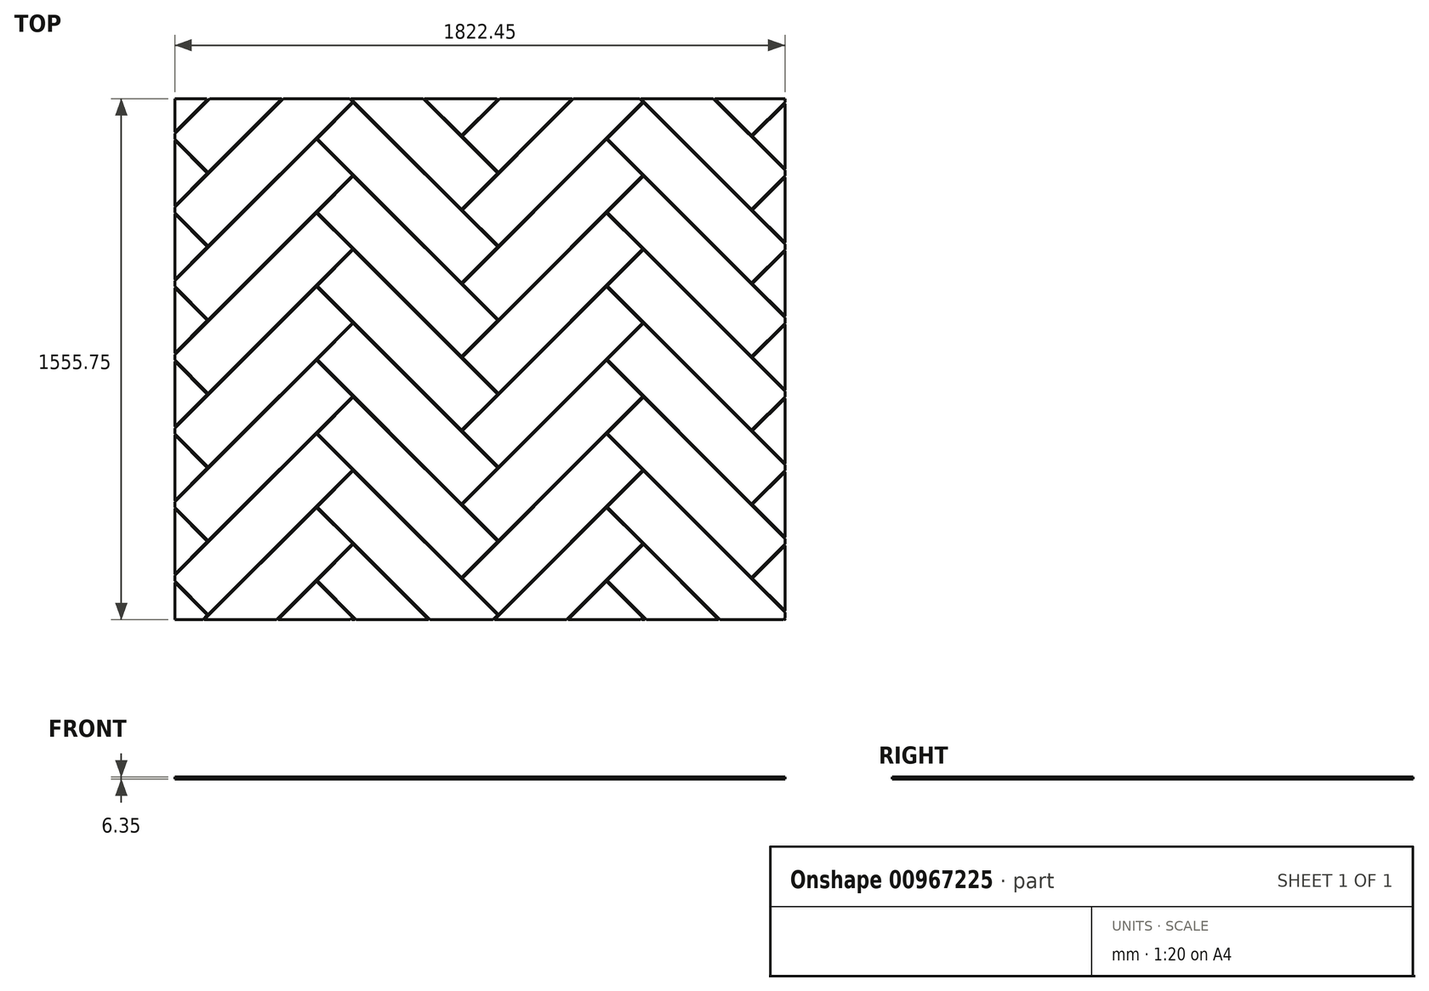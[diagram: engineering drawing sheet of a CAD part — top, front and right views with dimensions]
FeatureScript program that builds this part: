
annotation { "Feature Type Name" : "Feature", "Feature Type Description" : "" }
export const myFeature = defineFeature(function(context is Context, id is Id, definition is map)
    precondition{}
    {
        {
            var Q0;
            Q0=qCreatedBy(makeId("Top.planeOp"),FACE);
            var sketch = newSketch(context, id + "F0", { "sketchPlane" : qUnion([Q0])});
            skLineSegment(sketch, "E0.bottom", {"start": v(0, 0) * mm, "end": v(609.6, 0) * mm});
            skLineSegment(sketch, "E0.top", {"start": v(0, 152.4) * mm, "end": v(609.6, 152.4) * mm});
            skLineSegment(sketch, "E0.left", {"start": v(0, 0) * mm, "end": v(0, 152.4) * mm});
            skLineSegment(sketch, "E0.right", {"start": v(609.6, 0) * mm, "end": v(609.6, 152.4) * mm});
            skLineSegment(sketch, "E1.bottom", {"start": v(152.4, 155.57) * mm, "end": v(152.4, 765.17) * mm});
            skLineSegment(sketch, "E1.top", {"start": v(0, 155.58) * mm, "end": v(0, 765.17) * mm});
            skLineSegment(sketch, "E1.left", {"start": v(152.4, 155.57) * mm, "end": v(0, 155.57) * mm});
            skLineSegment(sketch, "E1.right", {"start": v(152.4, 765.17) * mm, "end": v(0, 765.17) * mm});
            skLineSegment(sketch, "E2.bottom", {"start": v(155.58, 155.57) * mm, "end": v(765.17, 155.57) * mm});
            skLineSegment(sketch, "E2.top", {"start": v(155.58, 307.98) * mm, "end": v(765.17, 307.97) * mm});
            skLineSegment(sketch, "E2.left", {"start": v(155.58, 155.58) * mm, "end": v(155.58, 307.98) * mm});
            skLineSegment(sketch, "E2.right", {"start": v(765.17, 155.57) * mm, "end": v(765.17, 307.97) * mm});
            skLineSegment(sketch, "E3.bottom", {"start": v(307.98, 311.15) * mm, "end": v(307.98, 920.75) * mm});
            skLineSegment(sketch, "E3.top", {"start": v(155.58, 311.15) * mm, "end": v(155.58, 920.75) * mm});
            skLineSegment(sketch, "E3.left", {"start": v(307.98, 311.15) * mm, "end": v(155.58, 311.15) * mm});
            skLineSegment(sketch, "E3.right", {"start": v(307.98, 920.75) * mm, "end": v(155.58, 920.75) * mm});
            skLineSegment(sketch, "E4.0.1.0", {"start": v(-612.78, 612.78) * mm, "end": v(-3.18, 612.78) * mm});
            skLineSegment(sketch, "E4.0.1.1", {"start": v(-460.37, 768.35) * mm, "end": v(-612.77, 768.35) * mm});
            skLineSegment(sketch, "E4.0.1.2", {"start": v(-457.2, 768.35) * mm, "end": v(-457.2, 920.75) * mm});
            skLineSegment(sketch, "E4.0.1.3", {"start": v(-304.8, 923.92) * mm, "end": v(-457.2, 923.92) * mm});
            skLineSegment(sketch, "E4.0.1.4", {"start": v(-457.2, 768.35) * mm, "end": v(152.4, 768.35) * mm});
            skLineSegment(sketch, "E4.0.1.5", {"start": v(-460.37, 768.35) * mm, "end": v(-460.37, 1377.95) * mm});
            skLineSegment(sketch, "E4.0.1.6", {"start": v(-457.2, 920.75) * mm, "end": v(152.4, 920.75) * mm});
            skLineSegment(sketch, "E4.0.1.7", {"start": v(-304.8, 1533.52) * mm, "end": v(-457.2, 1533.52) * mm});
            skLineSegment(sketch, "E4.0.1.8", {"start": v(-612.78, 768.35) * mm, "end": v(-612.77, 1377.95) * mm});
            skLineSegment(sketch, "E4.0.1.9", {"start": v(-457.2, 923.92) * mm, "end": v(-457.2, 1533.52) * mm});
            skLineSegment(sketch, "E4.0.1.10", {"start": v(-3.18, 612.78) * mm, "end": v(-3.18, 765.17) * mm});
            skLineSegment(sketch, "E4.0.1.11", {"start": v(-304.8, 923.92) * mm, "end": v(-304.8, 1533.52) * mm});
            skLineSegment(sketch, "E4.0.1.12", {"start": v(-612.78, 612.78) * mm, "end": v(-612.78, 765.17) * mm});
            skLineSegment(sketch, "E4.0.1.13", {"start": v(-460.37, 1377.95) * mm, "end": v(-612.77, 1377.95) * mm});
            skLineSegment(sketch, "E4.0.1.14", {"start": v(152.4, 768.35) * mm, "end": v(152.4, 920.75) * mm});
            skLineSegment(sketch, "E4.0.1.15", {"start": v(-612.77, 765.17) * mm, "end": v(-3.17, 765.17) * mm});
            skLineSegment(sketch, "E4.1.0.0", {"start": v(311.15, 311.15) * mm, "end": v(920.75, 311.15) * mm});
            skLineSegment(sketch, "E4.1.0.1", {"start": v(463.55, 466.72) * mm, "end": v(311.15, 466.72) * mm});
            skLineSegment(sketch, "E4.1.0.2", {"start": v(466.73, 466.72) * mm, "end": v(466.73, 619.12) * mm});
            skLineSegment(sketch, "E4.1.0.3", {"start": v(619.13, 622.3) * mm, "end": v(466.73, 622.3) * mm});
            skLineSegment(sketch, "E4.1.0.4", {"start": v(466.73, 466.72) * mm, "end": v(1076.33, 466.72) * mm});
            skLineSegment(sketch, "E4.1.0.5", {"start": v(463.55, 466.72) * mm, "end": v(463.55, 1076.32) * mm});
            skLineSegment(sketch, "E4.1.0.6", {"start": v(466.73, 619.12) * mm, "end": v(1076.33, 619.12) * mm});
            skLineSegment(sketch, "E4.1.0.7", {"start": v(619.13, 1231.9) * mm, "end": v(466.73, 1231.9) * mm});
            skLineSegment(sketch, "E4.1.0.8", {"start": v(311.15, 466.72) * mm, "end": v(311.15, 1076.32) * mm});
            skLineSegment(sketch, "E4.1.0.9", {"start": v(466.73, 622.3) * mm, "end": v(466.73, 1231.9) * mm});
            skLineSegment(sketch, "E4.1.0.10", {"start": v(920.75, 311.15) * mm, "end": v(920.75, 463.55) * mm});
            skLineSegment(sketch, "E4.1.0.11", {"start": v(619.13, 622.3) * mm, "end": v(619.13, 1231.9) * mm});
            skLineSegment(sketch, "E4.1.0.12", {"start": v(311.15, 311.15) * mm, "end": v(311.15, 463.55) * mm});
            skLineSegment(sketch, "E4.1.0.13", {"start": v(463.55, 1076.32) * mm, "end": v(311.15, 1076.32) * mm});
            skLineSegment(sketch, "E4.1.0.14", {"start": v(1076.32, 466.72) * mm, "end": v(1076.32, 619.12) * mm});
            skLineSegment(sketch, "E4.1.0.15", {"start": v(311.15, 463.55) * mm, "end": v(920.75, 463.55) * mm});
            skLineSegment(sketch, "E4.1.1.0", {"start": v(-301.62, 923.92) * mm, "end": v(307.98, 923.92) * mm});
            skLineSegment(sketch, "E4.1.1.1", {"start": v(-149.22, 1079.5) * mm, "end": v(-301.62, 1079.5) * mm});
            skLineSegment(sketch, "E4.1.1.2", {"start": v(-146.05, 1079.5) * mm, "end": v(-146.05, 1231.9) * mm});
            skLineSegment(sketch, "E4.1.1.3", {"start": v(6.35, 1235.07) * mm, "end": v(-146.05, 1235.07) * mm});
            skLineSegment(sketch, "E4.1.1.4", {"start": v(-146.05, 1079.5) * mm, "end": v(463.55, 1079.5) * mm});
            skLineSegment(sketch, "E4.1.1.5", {"start": v(-149.22, 1079.5) * mm, "end": v(-149.22, 1689.1) * mm});
            skLineSegment(sketch, "E4.1.1.6", {"start": v(-146.05, 1231.9) * mm, "end": v(463.55, 1231.9) * mm});
            skLineSegment(sketch, "E4.1.1.7", {"start": v(6.35, 1844.67) * mm, "end": v(-146.05, 1844.67) * mm});
            skLineSegment(sketch, "E4.1.1.8", {"start": v(-301.62, 1079.5) * mm, "end": v(-301.62, 1689.1) * mm});
            skLineSegment(sketch, "E4.1.1.9", {"start": v(-146.05, 1235.07) * mm, "end": v(-146.05, 1844.67) * mm});
            skLineSegment(sketch, "E4.1.1.10", {"start": v(307.98, 923.92) * mm, "end": v(307.98, 1076.32) * mm});
            skLineSegment(sketch, "E4.1.1.11", {"start": v(6.35, 1235.07) * mm, "end": v(6.35, 1844.67) * mm});
            skLineSegment(sketch, "E4.1.1.12", {"start": v(-301.62, 923.92) * mm, "end": v(-301.62, 1076.32) * mm});
            skLineSegment(sketch, "E4.1.1.13", {"start": v(-149.22, 1689.1) * mm, "end": v(-301.62, 1689.1) * mm});
            skLineSegment(sketch, "E4.1.1.14", {"start": v(463.55, 1079.5) * mm, "end": v(463.55, 1231.9) * mm});
            skLineSegment(sketch, "E4.1.1.15", {"start": v(-301.62, 1076.32) * mm, "end": v(307.98, 1076.32) * mm});
            skLineSegment(sketch, "E4.2.0.0", {"start": v(622.3, 622.3) * mm, "end": v(1231.9, 622.3) * mm});
            skLineSegment(sketch, "E4.2.0.1", {"start": v(774.7, 777.87) * mm, "end": v(622.3, 777.87) * mm});
            skLineSegment(sketch, "E4.2.0.2", {"start": v(777.88, 777.87) * mm, "end": v(777.88, 930.27) * mm});
            skLineSegment(sketch, "E4.2.0.3", {"start": v(930.28, 933.45) * mm, "end": v(777.88, 933.45) * mm});
            skLineSegment(sketch, "E4.2.0.4", {"start": v(777.88, 777.87) * mm, "end": v(1387.47, 777.87) * mm});
            skLineSegment(sketch, "E4.2.0.5", {"start": v(774.7, 777.87) * mm, "end": v(774.7, 1387.47) * mm});
            skLineSegment(sketch, "E4.2.0.6", {"start": v(777.88, 930.27) * mm, "end": v(1387.47, 930.27) * mm});
            skLineSegment(sketch, "E4.2.0.7", {"start": v(930.28, 1543.05) * mm, "end": v(777.88, 1543.05) * mm});
            skLineSegment(sketch, "E4.2.0.8", {"start": v(622.3, 777.87) * mm, "end": v(622.3, 1387.47) * mm});
            skLineSegment(sketch, "E4.2.0.9", {"start": v(777.88, 933.45) * mm, "end": v(777.88, 1543.05) * mm});
            skLineSegment(sketch, "E4.2.0.10", {"start": v(1231.9, 622.3) * mm, "end": v(1231.9, 774.7) * mm});
            skLineSegment(sketch, "E4.2.0.11", {"start": v(930.28, 933.45) * mm, "end": v(930.28, 1543.05) * mm});
            skLineSegment(sketch, "E4.2.0.12", {"start": v(622.3, 622.3) * mm, "end": v(622.3, 774.7) * mm});
            skLineSegment(sketch, "E4.2.0.13", {"start": v(774.7, 1387.47) * mm, "end": v(622.3, 1387.47) * mm});
            skLineSegment(sketch, "E4.2.0.14", {"start": v(1387.47, 777.87) * mm, "end": v(1387.47, 930.27) * mm});
            skLineSegment(sketch, "E4.2.0.15", {"start": v(622.3, 774.7) * mm, "end": v(1231.9, 774.7) * mm});
            skLineSegment(sketch, "E4.2.1.0", {"start": v(9.53, 1235.07) * mm, "end": v(619.13, 1235.07) * mm});
            skLineSegment(sketch, "E4.2.1.1", {"start": v(161.93, 1390.65) * mm, "end": v(9.53, 1390.65) * mm});
            skLineSegment(sketch, "E4.2.1.2", {"start": v(165.1, 1390.65) * mm, "end": v(165.1, 1543.05) * mm});
            skLineSegment(sketch, "E4.2.1.3", {"start": v(317.5, 1546.22) * mm, "end": v(165.1, 1546.22) * mm});
            skLineSegment(sketch, "E4.2.1.4", {"start": v(165.1, 1390.65) * mm, "end": v(774.7, 1390.65) * mm});
            skLineSegment(sketch, "E4.2.1.5", {"start": v(161.93, 1390.65) * mm, "end": v(161.93, 2000.25) * mm});
            skLineSegment(sketch, "E4.2.1.6", {"start": v(165.1, 1543.05) * mm, "end": v(774.7, 1543.05) * mm});
            skLineSegment(sketch, "E4.2.1.7", {"start": v(317.5, 2155.82) * mm, "end": v(165.1, 2155.82) * mm});
            skLineSegment(sketch, "E4.2.1.8", {"start": v(9.53, 1390.65) * mm, "end": v(9.53, 2000.25) * mm});
            skLineSegment(sketch, "E4.2.1.9", {"start": v(165.1, 1546.22) * mm, "end": v(165.1, 2155.82) * mm});
            skLineSegment(sketch, "E4.2.1.10", {"start": v(619.13, 1235.07) * mm, "end": v(619.13, 1387.47) * mm});
            skLineSegment(sketch, "E4.2.1.11", {"start": v(317.5, 1546.22) * mm, "end": v(317.5, 2155.82) * mm});
            skLineSegment(sketch, "E4.2.1.12", {"start": v(9.53, 1235.07) * mm, "end": v(9.53, 1387.47) * mm});
            skLineSegment(sketch, "E4.2.1.13", {"start": v(161.93, 2000.25) * mm, "end": v(9.53, 2000.25) * mm});
            skLineSegment(sketch, "E4.2.1.14", {"start": v(774.7, 1390.65) * mm, "end": v(774.7, 1543.05) * mm});
            skLineSegment(sketch, "E4.2.1.15", {"start": v(9.53, 1387.47) * mm, "end": v(619.13, 1387.47) * mm});
            skLineSegment(sketch, "E4.direction1", {"start": v(0, 0) * mm, "end": v(311.15, 311.15) * mm, "construction": true});
            skLineSegment(sketch, "E4.direction2", {"start": v(0, 0) * mm, "end": v(-612.78, 612.78) * mm, "construction": true});
            skLineSegment(sketch, "E5.0.3.0", {"start": v(933.45, 933.45) * mm, "end": v(1543.05, 933.45) * mm});
            skLineSegment(sketch, "E5.3.3.0", {"start": v(1085.85, 1089.02) * mm, "end": v(933.45, 1089.02) * mm});
            skLineSegment(sketch, "E5.6.3.0", {"start": v(1089.03, 1089.02) * mm, "end": v(1089.03, 1241.42) * mm});
            skLineSegment(sketch, "E5.9.3.0", {"start": v(1241.43, 1244.6) * mm, "end": v(1089.03, 1244.6) * mm});
            skLineSegment(sketch, "E5.12.3.0", {"start": v(1089.03, 1089.02) * mm, "end": v(1698.62, 1089.02) * mm});
            skLineSegment(sketch, "E5.15.3.0", {"start": v(1085.85, 1089.02) * mm, "end": v(1085.85, 1698.62) * mm});
            skLineSegment(sketch, "E5.18.3.0", {"start": v(1089.03, 1241.42) * mm, "end": v(1698.62, 1241.42) * mm});
            skLineSegment(sketch, "E5.21.3.0", {"start": v(1241.43, 1854.2) * mm, "end": v(1089.03, 1854.2) * mm});
            skLineSegment(sketch, "E5.24.3.0", {"start": v(933.45, 1089.02) * mm, "end": v(933.45, 1698.62) * mm});
            skLineSegment(sketch, "E5.27.3.0", {"start": v(1089.03, 1244.6) * mm, "end": v(1089.03, 1854.2) * mm});
            skLineSegment(sketch, "E5.30.3.0", {"start": v(1543.05, 933.45) * mm, "end": v(1543.05, 1085.85) * mm});
            skLineSegment(sketch, "E5.33.3.0", {"start": v(1241.43, 1244.6) * mm, "end": v(1241.43, 1854.2) * mm});
            skLineSegment(sketch, "E5.36.3.0", {"start": v(933.45, 933.45) * mm, "end": v(933.45, 1085.85) * mm});
            skLineSegment(sketch, "E5.39.3.0", {"start": v(1085.85, 1698.62) * mm, "end": v(933.45, 1698.62) * mm});
            skLineSegment(sketch, "E5.42.3.0", {"start": v(1698.62, 1089.02) * mm, "end": v(1698.62, 1241.42) * mm});
            skLineSegment(sketch, "E5.45.3.0", {"start": v(933.45, 1085.85) * mm, "end": v(1543.05, 1085.85) * mm});
            skLineSegment(sketch, "E5.0.3.1", {"start": v(320.68, 1546.22) * mm, "end": v(930.28, 1546.22) * mm});
            skLineSegment(sketch, "E5.3.3.1", {"start": v(473.08, 1701.8) * mm, "end": v(320.68, 1701.8) * mm});
            skLineSegment(sketch, "E5.6.3.1", {"start": v(476.25, 1701.8) * mm, "end": v(476.25, 1854.2) * mm});
            skLineSegment(sketch, "E5.9.3.1", {"start": v(628.65, 1857.37) * mm, "end": v(476.25, 1857.37) * mm});
            skLineSegment(sketch, "E5.12.3.1", {"start": v(476.25, 1701.8) * mm, "end": v(1085.85, 1701.8) * mm});
            skLineSegment(sketch, "E5.15.3.1", {"start": v(473.08, 1701.8) * mm, "end": v(473.08, 2311.4) * mm});
            skLineSegment(sketch, "E5.18.3.1", {"start": v(476.25, 1854.2) * mm, "end": v(1085.85, 1854.2) * mm});
            skLineSegment(sketch, "E5.21.3.1", {"start": v(628.65, 2466.97) * mm, "end": v(476.25, 2466.97) * mm});
            skLineSegment(sketch, "E5.24.3.1", {"start": v(320.68, 1701.8) * mm, "end": v(320.68, 2311.4) * mm});
            skLineSegment(sketch, "E5.27.3.1", {"start": v(476.25, 1857.37) * mm, "end": v(476.25, 2466.97) * mm});
            skLineSegment(sketch, "E5.30.3.1", {"start": v(930.28, 1546.22) * mm, "end": v(930.28, 1698.62) * mm});
            skLineSegment(sketch, "E5.33.3.1", {"start": v(628.65, 1857.37) * mm, "end": v(628.65, 2466.97) * mm});
            skLineSegment(sketch, "E5.36.3.1", {"start": v(320.68, 1546.22) * mm, "end": v(320.68, 1698.62) * mm});
            skLineSegment(sketch, "E5.39.3.1", {"start": v(473.08, 2311.4) * mm, "end": v(320.68, 2311.4) * mm});
            skLineSegment(sketch, "E5.42.3.1", {"start": v(1085.85, 1701.8) * mm, "end": v(1085.85, 1854.2) * mm});
            skLineSegment(sketch, "E5.45.3.1", {"start": v(320.68, 1698.62) * mm, "end": v(930.28, 1698.62) * mm});
            skLineSegment(sketch, "E5.0.4.0", {"start": v(1244.6, 1244.6) * mm, "end": v(1854.2, 1244.6) * mm});
            skLineSegment(sketch, "E5.3.4.0", {"start": v(1397, 1400.17) * mm, "end": v(1244.6, 1400.17) * mm});
            skLineSegment(sketch, "E5.6.4.0", {"start": v(1400.18, 1400.17) * mm, "end": v(1400.18, 1552.57) * mm});
            skLineSegment(sketch, "E5.9.4.0", {"start": v(1552.58, 1555.75) * mm, "end": v(1400.18, 1555.75) * mm});
            skLineSegment(sketch, "E5.12.4.0", {"start": v(1400.18, 1400.17) * mm, "end": v(2009.78, 1400.17) * mm});
            skLineSegment(sketch, "E5.15.4.0", {"start": v(1397, 1400.17) * mm, "end": v(1397, 2009.77) * mm});
            skLineSegment(sketch, "E5.18.4.0", {"start": v(1400.18, 1552.57) * mm, "end": v(2009.78, 1552.57) * mm});
            skLineSegment(sketch, "E5.21.4.0", {"start": v(1552.58, 2165.35) * mm, "end": v(1400.18, 2165.35) * mm});
            skLineSegment(sketch, "E5.24.4.0", {"start": v(1244.6, 1400.17) * mm, "end": v(1244.6, 2009.77) * mm});
            skLineSegment(sketch, "E5.27.4.0", {"start": v(1400.18, 1555.75) * mm, "end": v(1400.18, 2165.35) * mm});
            skLineSegment(sketch, "E5.30.4.0", {"start": v(1854.2, 1244.6) * mm, "end": v(1854.2, 1397) * mm});
            skLineSegment(sketch, "E5.33.4.0", {"start": v(1552.58, 1555.75) * mm, "end": v(1552.58, 2165.35) * mm});
            skLineSegment(sketch, "E5.36.4.0", {"start": v(1244.6, 1244.6) * mm, "end": v(1244.6, 1397) * mm});
            skLineSegment(sketch, "E5.39.4.0", {"start": v(1397, 2009.77) * mm, "end": v(1244.6, 2009.77) * mm});
            skLineSegment(sketch, "E5.42.4.0", {"start": v(2009.78, 1400.17) * mm, "end": v(2009.78, 1552.57) * mm});
            skLineSegment(sketch, "E5.45.4.0", {"start": v(1244.6, 1397) * mm, "end": v(1854.2, 1397) * mm});
            skLineSegment(sketch, "E5.0.4.1", {"start": v(631.83, 1857.37) * mm, "end": v(1241.43, 1857.37) * mm});
            skLineSegment(sketch, "E5.3.4.1", {"start": v(784.23, 2012.95) * mm, "end": v(631.83, 2012.95) * mm});
            skLineSegment(sketch, "E5.6.4.1", {"start": v(787.4, 2012.95) * mm, "end": v(787.4, 2165.35) * mm});
            skLineSegment(sketch, "E5.9.4.1", {"start": v(939.8, 2168.52) * mm, "end": v(787.4, 2168.52) * mm});
            skLineSegment(sketch, "E5.12.4.1", {"start": v(787.4, 2012.95) * mm, "end": v(1397, 2012.95) * mm});
            skLineSegment(sketch, "E5.15.4.1", {"start": v(784.23, 2012.95) * mm, "end": v(784.23, 2622.55) * mm});
            skLineSegment(sketch, "E5.18.4.1", {"start": v(787.4, 2165.35) * mm, "end": v(1397, 2165.35) * mm});
            skLineSegment(sketch, "E5.21.4.1", {"start": v(939.8, 2778.12) * mm, "end": v(787.4, 2778.12) * mm});
            skLineSegment(sketch, "E5.24.4.1", {"start": v(631.83, 2012.95) * mm, "end": v(631.83, 2622.55) * mm});
            skLineSegment(sketch, "E5.27.4.1", {"start": v(787.4, 2168.52) * mm, "end": v(787.4, 2778.12) * mm});
            skLineSegment(sketch, "E5.30.4.1", {"start": v(1241.43, 1857.37) * mm, "end": v(1241.43, 2009.77) * mm});
            skLineSegment(sketch, "E5.33.4.1", {"start": v(939.8, 2168.52) * mm, "end": v(939.8, 2778.12) * mm});
            skLineSegment(sketch, "E5.36.4.1", {"start": v(631.83, 1857.37) * mm, "end": v(631.83, 2009.77) * mm});
            skLineSegment(sketch, "E5.39.4.1", {"start": v(784.23, 2622.55) * mm, "end": v(631.83, 2622.55) * mm});
            skLineSegment(sketch, "E5.42.4.1", {"start": v(1397, 2012.95) * mm, "end": v(1397, 2165.35) * mm});
            skLineSegment(sketch, "E5.45.4.1", {"start": v(631.83, 2009.77) * mm, "end": v(1241.43, 2009.77) * mm});
            skLineSegment(sketch, "E5.0.5.0", {"start": v(1555.75, 1555.75) * mm, "end": v(2165.35, 1555.75) * mm});
            skLineSegment(sketch, "E5.3.5.0", {"start": v(1708.15, 1711.32) * mm, "end": v(1555.75, 1711.32) * mm});
            skLineSegment(sketch, "E5.6.5.0", {"start": v(1711.33, 1711.32) * mm, "end": v(1711.33, 1863.72) * mm});
            skLineSegment(sketch, "E5.9.5.0", {"start": v(1863.73, 1866.9) * mm, "end": v(1711.33, 1866.9) * mm});
            skLineSegment(sketch, "E5.12.5.0", {"start": v(1711.33, 1711.32) * mm, "end": v(2320.92, 1711.32) * mm});
            skLineSegment(sketch, "E5.15.5.0", {"start": v(1708.15, 1711.32) * mm, "end": v(1708.15, 2320.92) * mm});
            skLineSegment(sketch, "E5.18.5.0", {"start": v(1711.33, 1863.72) * mm, "end": v(2320.92, 1863.72) * mm});
            skLineSegment(sketch, "E5.21.5.0", {"start": v(1863.73, 2476.5) * mm, "end": v(1711.33, 2476.5) * mm});
            skLineSegment(sketch, "E5.24.5.0", {"start": v(1555.75, 1711.32) * mm, "end": v(1555.75, 2320.92) * mm});
            skLineSegment(sketch, "E5.27.5.0", {"start": v(1711.33, 1866.9) * mm, "end": v(1711.33, 2476.5) * mm});
            skLineSegment(sketch, "E5.30.5.0", {"start": v(2165.35, 1555.75) * mm, "end": v(2165.35, 1708.15) * mm});
            skLineSegment(sketch, "E5.33.5.0", {"start": v(1863.73, 1866.9) * mm, "end": v(1863.73, 2476.5) * mm});
            skLineSegment(sketch, "E5.36.5.0", {"start": v(1555.75, 1555.75) * mm, "end": v(1555.75, 1708.15) * mm});
            skLineSegment(sketch, "E5.39.5.0", {"start": v(1708.15, 2320.92) * mm, "end": v(1555.75, 2320.92) * mm});
            skLineSegment(sketch, "E5.42.5.0", {"start": v(2320.92, 1711.32) * mm, "end": v(2320.92, 1863.72) * mm});
            skLineSegment(sketch, "E5.45.5.0", {"start": v(1555.75, 1708.15) * mm, "end": v(2165.35, 1708.15) * mm});
            skLineSegment(sketch, "E5.0.5.1", {"start": v(942.98, 2168.52) * mm, "end": v(1552.58, 2168.52) * mm});
            skLineSegment(sketch, "E5.3.5.1", {"start": v(1095.38, 2324.1) * mm, "end": v(942.98, 2324.1) * mm});
            skLineSegment(sketch, "E5.6.5.1", {"start": v(1098.55, 2324.1) * mm, "end": v(1098.55, 2476.5) * mm});
            skLineSegment(sketch, "E5.9.5.1", {"start": v(1250.95, 2479.67) * mm, "end": v(1098.55, 2479.67) * mm});
            skLineSegment(sketch, "E5.12.5.1", {"start": v(1098.55, 2324.1) * mm, "end": v(1708.15, 2324.1) * mm});
            skLineSegment(sketch, "E5.15.5.1", {"start": v(1095.38, 2324.1) * mm, "end": v(1095.38, 2933.7) * mm});
            skLineSegment(sketch, "E5.18.5.1", {"start": v(1098.55, 2476.5) * mm, "end": v(1708.15, 2476.5) * mm});
            skLineSegment(sketch, "E5.21.5.1", {"start": v(1250.95, 3089.27) * mm, "end": v(1098.55, 3089.27) * mm});
            skLineSegment(sketch, "E5.24.5.1", {"start": v(942.98, 2324.1) * mm, "end": v(942.98, 2933.7) * mm});
            skLineSegment(sketch, "E5.27.5.1", {"start": v(1098.55, 2479.67) * mm, "end": v(1098.55, 3089.27) * mm});
            skLineSegment(sketch, "E5.30.5.1", {"start": v(1552.58, 2168.52) * mm, "end": v(1552.58, 2320.92) * mm});
            skLineSegment(sketch, "E5.33.5.1", {"start": v(1250.95, 2479.67) * mm, "end": v(1250.95, 3089.27) * mm});
            skLineSegment(sketch, "E5.36.5.1", {"start": v(942.98, 2168.52) * mm, "end": v(942.98, 2320.92) * mm});
            skLineSegment(sketch, "E5.39.5.1", {"start": v(1095.38, 2933.7) * mm, "end": v(942.98, 2933.7) * mm});
            skLineSegment(sketch, "E5.42.5.1", {"start": v(1708.15, 2324.1) * mm, "end": v(1708.15, 2476.5) * mm});
            skLineSegment(sketch, "E5.45.5.1", {"start": v(942.98, 2320.92) * mm, "end": v(1552.58, 2320.92) * mm});
            skLineSegment(sketch, "E6.0.0.2", {"start": v(-1225.55, 1225.55) * mm, "end": v(-615.95, 1225.55) * mm});
            skLineSegment(sketch, "E6.3.0.2", {"start": v(-1073.15, 1381.12) * mm, "end": v(-1225.55, 1381.12) * mm});
            skLineSegment(sketch, "E6.6.0.2", {"start": v(-1069.97, 1381.12) * mm, "end": v(-1069.97, 1533.52) * mm});
            skLineSegment(sketch, "E6.9.0.2", {"start": v(-917.57, 1536.7) * mm, "end": v(-1069.97, 1536.7) * mm});
            skLineSegment(sketch, "E6.12.0.2", {"start": v(-1069.97, 1381.12) * mm, "end": v(-460.37, 1381.12) * mm});
            skLineSegment(sketch, "E6.15.0.2", {"start": v(-1073.15, 1381.12) * mm, "end": v(-1073.15, 1990.72) * mm});
            skLineSegment(sketch, "E6.18.0.2", {"start": v(-1069.97, 1533.52) * mm, "end": v(-460.37, 1533.52) * mm});
            skLineSegment(sketch, "E6.21.0.2", {"start": v(-917.57, 2146.3) * mm, "end": v(-1069.97, 2146.3) * mm});
            skLineSegment(sketch, "E6.24.0.2", {"start": v(-1225.55, 1381.12) * mm, "end": v(-1225.55, 1990.72) * mm});
            skLineSegment(sketch, "E6.27.0.2", {"start": v(-1069.97, 1536.7) * mm, "end": v(-1069.97, 2146.3) * mm});
            skLineSegment(sketch, "E6.30.0.2", {"start": v(-615.95, 1225.55) * mm, "end": v(-615.95, 1377.95) * mm});
            skLineSegment(sketch, "E6.33.0.2", {"start": v(-917.57, 1536.7) * mm, "end": v(-917.57, 2146.3) * mm});
            skLineSegment(sketch, "E6.36.0.2", {"start": v(-1225.55, 1225.55) * mm, "end": v(-1225.55, 1377.95) * mm});
            skLineSegment(sketch, "E6.39.0.2", {"start": v(-1073.15, 1990.72) * mm, "end": v(-1225.55, 1990.72) * mm});
            skLineSegment(sketch, "E6.42.0.2", {"start": v(-460.37, 1381.12) * mm, "end": v(-460.37, 1533.52) * mm});
            skLineSegment(sketch, "E6.45.0.2", {"start": v(-1225.55, 1377.95) * mm, "end": v(-615.95, 1377.95) * mm});
            skLineSegment(sketch, "E6.0.0.3", {"start": v(-1838.33, 1838.33) * mm, "end": v(-1228.73, 1838.33) * mm});
            skLineSegment(sketch, "E6.3.0.3", {"start": v(-1685.92, 1993.9) * mm, "end": v(-1838.32, 1993.9) * mm});
            skLineSegment(sketch, "E6.6.0.3", {"start": v(-1682.75, 1993.9) * mm, "end": v(-1682.75, 2146.3) * mm});
            skLineSegment(sketch, "E6.9.0.3", {"start": v(-1530.35, 2149.47) * mm, "end": v(-1682.75, 2149.47) * mm});
            skLineSegment(sketch, "E6.12.0.3", {"start": v(-1682.75, 1993.9) * mm, "end": v(-1073.15, 1993.9) * mm});
            skLineSegment(sketch, "E6.15.0.3", {"start": v(-1685.92, 1993.9) * mm, "end": v(-1685.92, 2603.5) * mm});
            skLineSegment(sketch, "E6.18.0.3", {"start": v(-1682.75, 2146.3) * mm, "end": v(-1073.15, 2146.3) * mm});
            skLineSegment(sketch, "E6.21.0.3", {"start": v(-1530.35, 2759.07) * mm, "end": v(-1682.75, 2759.07) * mm});
            skLineSegment(sketch, "E6.24.0.3", {"start": v(-1838.33, 1993.9) * mm, "end": v(-1838.33, 2603.5) * mm});
            skLineSegment(sketch, "E6.27.0.3", {"start": v(-1682.75, 2149.47) * mm, "end": v(-1682.75, 2759.07) * mm});
            skLineSegment(sketch, "E6.30.0.3", {"start": v(-1228.73, 1838.33) * mm, "end": v(-1228.73, 1990.72) * mm});
            skLineSegment(sketch, "E6.33.0.3", {"start": v(-1530.35, 2149.47) * mm, "end": v(-1530.35, 2759.07) * mm});
            skLineSegment(sketch, "E6.36.0.3", {"start": v(-1838.33, 1838.33) * mm, "end": v(-1838.33, 1990.72) * mm});
            skLineSegment(sketch, "E6.39.0.3", {"start": v(-1685.92, 2603.5) * mm, "end": v(-1838.32, 2603.5) * mm});
            skLineSegment(sketch, "E6.42.0.3", {"start": v(-1073.15, 1993.9) * mm, "end": v(-1073.15, 2146.3) * mm});
            skLineSegment(sketch, "E6.45.0.3", {"start": v(-1838.32, 1990.72) * mm, "end": v(-1228.72, 1990.72) * mm});
            skLineSegment(sketch, "E6.0.0.4", {"start": v(-2451.1, 2451.1) * mm, "end": v(-1841.5, 2451.1) * mm});
            skLineSegment(sketch, "E6.3.0.4", {"start": v(-2298.7, 2606.67) * mm, "end": v(-2451.1, 2606.67) * mm});
            skLineSegment(sketch, "E6.6.0.4", {"start": v(-2295.52, 2606.67) * mm, "end": v(-2295.52, 2759.07) * mm});
            skLineSegment(sketch, "E6.9.0.4", {"start": v(-2143.12, 2762.25) * mm, "end": v(-2295.52, 2762.25) * mm});
            skLineSegment(sketch, "E6.12.0.4", {"start": v(-2295.52, 2606.67) * mm, "end": v(-1685.92, 2606.67) * mm});
            skLineSegment(sketch, "E6.15.0.4", {"start": v(-2298.7, 2606.67) * mm, "end": v(-2298.7, 3216.27) * mm});
            skLineSegment(sketch, "E6.18.0.4", {"start": v(-2295.52, 2759.07) * mm, "end": v(-1685.92, 2759.07) * mm});
            skLineSegment(sketch, "E6.21.0.4", {"start": v(-2143.12, 3371.85) * mm, "end": v(-2295.52, 3371.85) * mm});
            skLineSegment(sketch, "E6.24.0.4", {"start": v(-2451.1, 2606.67) * mm, "end": v(-2451.1, 3216.27) * mm});
            skLineSegment(sketch, "E6.27.0.4", {"start": v(-2295.52, 2762.25) * mm, "end": v(-2295.52, 3371.85) * mm});
            skLineSegment(sketch, "E6.30.0.4", {"start": v(-1841.5, 2451.1) * mm, "end": v(-1841.5, 2603.5) * mm});
            skLineSegment(sketch, "E6.33.0.4", {"start": v(-2143.12, 2762.25) * mm, "end": v(-2143.12, 3371.85) * mm});
            skLineSegment(sketch, "E6.36.0.4", {"start": v(-2451.1, 2451.1) * mm, "end": v(-2451.1, 2603.5) * mm});
            skLineSegment(sketch, "E6.39.0.4", {"start": v(-2298.7, 3216.27) * mm, "end": v(-2451.1, 3216.27) * mm});
            skLineSegment(sketch, "E6.42.0.4", {"start": v(-1685.92, 2606.67) * mm, "end": v(-1685.92, 2759.07) * mm});
            skLineSegment(sketch, "E6.45.0.4", {"start": v(-2451.1, 2603.5) * mm, "end": v(-1841.5, 2603.5) * mm});
            skLineSegment(sketch, "E6.0.1.2", {"start": v(-914.4, 1536.7) * mm, "end": v(-304.8, 1536.7) * mm});
            skLineSegment(sketch, "E6.3.1.2", {"start": v(-762, 1692.27) * mm, "end": v(-914.4, 1692.27) * mm});
            skLineSegment(sketch, "E6.6.1.2", {"start": v(-758.82, 1692.27) * mm, "end": v(-758.82, 1844.67) * mm});
            skLineSegment(sketch, "E6.9.1.2", {"start": v(-606.42, 1847.85) * mm, "end": v(-758.82, 1847.85) * mm});
            skLineSegment(sketch, "E6.12.1.2", {"start": v(-758.82, 1692.27) * mm, "end": v(-149.22, 1692.27) * mm});
            skLineSegment(sketch, "E6.15.1.2", {"start": v(-762, 1692.27) * mm, "end": v(-762, 2301.87) * mm});
            skLineSegment(sketch, "E6.18.1.2", {"start": v(-758.82, 1844.67) * mm, "end": v(-149.22, 1844.67) * mm});
            skLineSegment(sketch, "E6.21.1.2", {"start": v(-606.42, 2457.45) * mm, "end": v(-758.82, 2457.45) * mm});
            skLineSegment(sketch, "E6.24.1.2", {"start": v(-914.4, 1692.27) * mm, "end": v(-914.4, 2301.87) * mm});
            skLineSegment(sketch, "E6.27.1.2", {"start": v(-758.82, 1847.85) * mm, "end": v(-758.82, 2457.45) * mm});
            skLineSegment(sketch, "E6.30.1.2", {"start": v(-304.8, 1536.7) * mm, "end": v(-304.8, 1689.1) * mm});
            skLineSegment(sketch, "E6.33.1.2", {"start": v(-606.42, 1847.85) * mm, "end": v(-606.42, 2457.45) * mm});
            skLineSegment(sketch, "E6.36.1.2", {"start": v(-914.4, 1536.7) * mm, "end": v(-914.4, 1689.1) * mm});
            skLineSegment(sketch, "E6.39.1.2", {"start": v(-762, 2301.87) * mm, "end": v(-914.4, 2301.87) * mm});
            skLineSegment(sketch, "E6.42.1.2", {"start": v(-149.22, 1692.27) * mm, "end": v(-149.22, 1844.67) * mm});
            skLineSegment(sketch, "E6.45.1.2", {"start": v(-914.4, 1689.1) * mm, "end": v(-304.8, 1689.1) * mm});
            skLineSegment(sketch, "E6.0.1.3", {"start": v(-1527.17, 2149.47) * mm, "end": v(-917.57, 2149.47) * mm});
            skLineSegment(sketch, "E6.3.1.3", {"start": v(-1374.77, 2305.05) * mm, "end": v(-1527.17, 2305.05) * mm});
            skLineSegment(sketch, "E6.6.1.3", {"start": v(-1371.6, 2305.05) * mm, "end": v(-1371.6, 2457.45) * mm});
            skLineSegment(sketch, "E6.9.1.3", {"start": v(-1219.2, 2460.62) * mm, "end": v(-1371.6, 2460.62) * mm});
            skLineSegment(sketch, "E6.12.1.3", {"start": v(-1371.6, 2305.05) * mm, "end": v(-762, 2305.05) * mm});
            skLineSegment(sketch, "E6.15.1.3", {"start": v(-1374.77, 2305.05) * mm, "end": v(-1374.77, 2914.65) * mm});
            skLineSegment(sketch, "E6.18.1.3", {"start": v(-1371.6, 2457.45) * mm, "end": v(-762, 2457.45) * mm});
            skLineSegment(sketch, "E6.21.1.3", {"start": v(-1219.2, 3070.22) * mm, "end": v(-1371.6, 3070.22) * mm});
            skLineSegment(sketch, "E6.24.1.3", {"start": v(-1527.17, 2305.05) * mm, "end": v(-1527.17, 2914.65) * mm});
            skLineSegment(sketch, "E6.27.1.3", {"start": v(-1371.6, 2460.62) * mm, "end": v(-1371.6, 3070.22) * mm});
            skLineSegment(sketch, "E6.30.1.3", {"start": v(-917.57, 2149.47) * mm, "end": v(-917.57, 2301.87) * mm});
            skLineSegment(sketch, "E6.33.1.3", {"start": v(-1219.2, 2460.62) * mm, "end": v(-1219.2, 3070.22) * mm});
            skLineSegment(sketch, "E6.36.1.3", {"start": v(-1527.17, 2149.47) * mm, "end": v(-1527.17, 2301.87) * mm});
            skLineSegment(sketch, "E6.39.1.3", {"start": v(-1374.77, 2914.65) * mm, "end": v(-1527.17, 2914.65) * mm});
            skLineSegment(sketch, "E6.42.1.3", {"start": v(-762, 2305.05) * mm, "end": v(-762, 2457.45) * mm});
            skLineSegment(sketch, "E6.45.1.3", {"start": v(-1527.17, 2301.87) * mm, "end": v(-917.57, 2301.87) * mm});
            skLineSegment(sketch, "E6.0.1.4", {"start": v(-2139.95, 2762.25) * mm, "end": v(-1530.35, 2762.25) * mm});
            skLineSegment(sketch, "E6.3.1.4", {"start": v(-1987.55, 2917.82) * mm, "end": v(-2139.95, 2917.82) * mm});
            skLineSegment(sketch, "E6.6.1.4", {"start": v(-1984.37, 2917.82) * mm, "end": v(-1984.37, 3070.22) * mm});
            skLineSegment(sketch, "E6.9.1.4", {"start": v(-1831.97, 3073.4) * mm, "end": v(-1984.37, 3073.4) * mm});
            skLineSegment(sketch, "E6.12.1.4", {"start": v(-1984.37, 2917.82) * mm, "end": v(-1374.77, 2917.82) * mm});
            skLineSegment(sketch, "E6.15.1.4", {"start": v(-1987.55, 2917.82) * mm, "end": v(-1987.55, 3527.42) * mm});
            skLineSegment(sketch, "E6.18.1.4", {"start": v(-1984.37, 3070.22) * mm, "end": v(-1374.77, 3070.22) * mm});
            skLineSegment(sketch, "E6.21.1.4", {"start": v(-1831.97, 3683) * mm, "end": v(-1984.37, 3683) * mm});
            skLineSegment(sketch, "E6.24.1.4", {"start": v(-2139.95, 2917.82) * mm, "end": v(-2139.95, 3527.42) * mm});
            skLineSegment(sketch, "E6.27.1.4", {"start": v(-1984.37, 3073.4) * mm, "end": v(-1984.37, 3683) * mm});
            skLineSegment(sketch, "E6.30.1.4", {"start": v(-1530.35, 2762.25) * mm, "end": v(-1530.35, 2914.65) * mm});
            skLineSegment(sketch, "E6.33.1.4", {"start": v(-1831.97, 3073.4) * mm, "end": v(-1831.97, 3683) * mm});
            skLineSegment(sketch, "E6.36.1.4", {"start": v(-2139.95, 2762.25) * mm, "end": v(-2139.95, 2914.65) * mm});
            skLineSegment(sketch, "E6.39.1.4", {"start": v(-1987.55, 3527.42) * mm, "end": v(-2139.95, 3527.42) * mm});
            skLineSegment(sketch, "E6.42.1.4", {"start": v(-1374.77, 2917.82) * mm, "end": v(-1374.77, 3070.22) * mm});
            skLineSegment(sketch, "E6.45.1.4", {"start": v(-2139.95, 2914.65) * mm, "end": v(-1530.35, 2914.65) * mm});
            skLineSegment(sketch, "E6.0.2.2", {"start": v(-603.25, 1847.85) * mm, "end": v(6.35, 1847.85) * mm});
            skLineSegment(sketch, "E6.3.2.2", {"start": v(-450.85, 2003.42) * mm, "end": v(-603.25, 2003.42) * mm});
            skLineSegment(sketch, "E6.6.2.2", {"start": v(-447.67, 2003.42) * mm, "end": v(-447.67, 2155.82) * mm});
            skLineSegment(sketch, "E6.9.2.2", {"start": v(-295.27, 2159) * mm, "end": v(-447.67, 2159) * mm});
            skLineSegment(sketch, "E6.12.2.2", {"start": v(-447.67, 2003.42) * mm, "end": v(161.93, 2003.42) * mm});
            skLineSegment(sketch, "E6.15.2.2", {"start": v(-450.85, 2003.42) * mm, "end": v(-450.85, 2613.02) * mm});
            skLineSegment(sketch, "E6.18.2.2", {"start": v(-447.67, 2155.82) * mm, "end": v(161.93, 2155.82) * mm});
            skLineSegment(sketch, "E6.21.2.2", {"start": v(-295.27, 2768.6) * mm, "end": v(-447.67, 2768.6) * mm});
            skLineSegment(sketch, "E6.24.2.2", {"start": v(-603.25, 2003.42) * mm, "end": v(-603.25, 2613.02) * mm});
            skLineSegment(sketch, "E6.27.2.2", {"start": v(-447.67, 2159) * mm, "end": v(-447.67, 2768.6) * mm});
            skLineSegment(sketch, "E6.30.2.2", {"start": v(6.35, 1847.85) * mm, "end": v(6.35, 2000.25) * mm});
            skLineSegment(sketch, "E6.33.2.2", {"start": v(-295.27, 2159) * mm, "end": v(-295.27, 2768.6) * mm});
            skLineSegment(sketch, "E6.36.2.2", {"start": v(-603.25, 1847.85) * mm, "end": v(-603.25, 2000.25) * mm});
            skLineSegment(sketch, "E6.39.2.2", {"start": v(-450.85, 2613.02) * mm, "end": v(-603.25, 2613.02) * mm});
            skLineSegment(sketch, "E6.42.2.2", {"start": v(161.93, 2003.42) * mm, "end": v(161.93, 2155.82) * mm});
            skLineSegment(sketch, "E6.45.2.2", {"start": v(-603.25, 2000.25) * mm, "end": v(6.35, 2000.25) * mm});
            skLineSegment(sketch, "E6.0.2.3", {"start": v(-1216.02, 2460.62) * mm, "end": v(-606.42, 2460.62) * mm});
            skLineSegment(sketch, "E6.3.2.3", {"start": v(-1063.62, 2616.2) * mm, "end": v(-1216.02, 2616.2) * mm});
            skLineSegment(sketch, "E6.6.2.3", {"start": v(-1060.45, 2616.2) * mm, "end": v(-1060.45, 2768.6) * mm});
            skLineSegment(sketch, "E6.9.2.3", {"start": v(-908.05, 2771.77) * mm, "end": v(-1060.45, 2771.77) * mm});
            skLineSegment(sketch, "E6.12.2.3", {"start": v(-1060.45, 2616.2) * mm, "end": v(-450.85, 2616.2) * mm});
            skLineSegment(sketch, "E6.15.2.3", {"start": v(-1063.62, 2616.2) * mm, "end": v(-1063.62, 3225.8) * mm});
            skLineSegment(sketch, "E6.18.2.3", {"start": v(-1060.45, 2768.6) * mm, "end": v(-450.85, 2768.6) * mm});
            skLineSegment(sketch, "E6.21.2.3", {"start": v(-908.05, 3381.37) * mm, "end": v(-1060.45, 3381.37) * mm});
            skLineSegment(sketch, "E6.24.2.3", {"start": v(-1216.02, 2616.2) * mm, "end": v(-1216.02, 3225.8) * mm});
            skLineSegment(sketch, "E6.27.2.3", {"start": v(-1060.45, 2771.77) * mm, "end": v(-1060.45, 3381.37) * mm});
            skLineSegment(sketch, "E6.30.2.3", {"start": v(-606.42, 2460.62) * mm, "end": v(-606.42, 2613.02) * mm});
            skLineSegment(sketch, "E6.33.2.3", {"start": v(-908.05, 2771.77) * mm, "end": v(-908.05, 3381.37) * mm});
            skLineSegment(sketch, "E6.36.2.3", {"start": v(-1216.02, 2460.62) * mm, "end": v(-1216.02, 2613.02) * mm});
            skLineSegment(sketch, "E6.39.2.3", {"start": v(-1063.62, 3225.8) * mm, "end": v(-1216.02, 3225.8) * mm});
            skLineSegment(sketch, "E6.42.2.3", {"start": v(-450.85, 2616.2) * mm, "end": v(-450.85, 2768.6) * mm});
            skLineSegment(sketch, "E6.45.2.3", {"start": v(-1216.02, 2613.02) * mm, "end": v(-606.42, 2613.02) * mm});
            skLineSegment(sketch, "E6.0.2.4", {"start": v(-1828.8, 3073.4) * mm, "end": v(-1219.2, 3073.4) * mm});
            skLineSegment(sketch, "E6.3.2.4", {"start": v(-1676.4, 3228.97) * mm, "end": v(-1828.8, 3228.97) * mm});
            skLineSegment(sketch, "E6.6.2.4", {"start": v(-1673.22, 3228.97) * mm, "end": v(-1673.22, 3381.37) * mm});
            skLineSegment(sketch, "E6.9.2.4", {"start": v(-1520.82, 3384.55) * mm, "end": v(-1673.22, 3384.55) * mm});
            skLineSegment(sketch, "E6.12.2.4", {"start": v(-1673.22, 3228.97) * mm, "end": v(-1063.62, 3228.97) * mm});
            skLineSegment(sketch, "E6.15.2.4", {"start": v(-1676.4, 3228.97) * mm, "end": v(-1676.4, 3838.57) * mm});
            skLineSegment(sketch, "E6.18.2.4", {"start": v(-1673.22, 3381.37) * mm, "end": v(-1063.62, 3381.37) * mm});
            skLineSegment(sketch, "E6.21.2.4", {"start": v(-1520.82, 3994.15) * mm, "end": v(-1673.22, 3994.15) * mm});
            skLineSegment(sketch, "E6.24.2.4", {"start": v(-1828.8, 3228.97) * mm, "end": v(-1828.8, 3838.57) * mm});
            skLineSegment(sketch, "E6.27.2.4", {"start": v(-1673.22, 3384.55) * mm, "end": v(-1673.22, 3994.15) * mm});
            skLineSegment(sketch, "E6.30.2.4", {"start": v(-1219.2, 3073.4) * mm, "end": v(-1219.2, 3225.8) * mm});
            skLineSegment(sketch, "E6.33.2.4", {"start": v(-1520.82, 3384.55) * mm, "end": v(-1520.82, 3994.15) * mm});
            skLineSegment(sketch, "E6.36.2.4", {"start": v(-1828.8, 3073.4) * mm, "end": v(-1828.8, 3225.8) * mm});
            skLineSegment(sketch, "E6.39.2.4", {"start": v(-1676.4, 3838.57) * mm, "end": v(-1828.8, 3838.57) * mm});
            skLineSegment(sketch, "E6.42.2.4", {"start": v(-1063.62, 3228.97) * mm, "end": v(-1063.62, 3381.37) * mm});
            skLineSegment(sketch, "E6.45.2.4", {"start": v(-1828.8, 3225.8) * mm, "end": v(-1219.2, 3225.8) * mm});
            skLineSegment(sketch, "E6.0.3.2", {"start": v(-292.1, 2159) * mm, "end": v(317.5, 2159) * mm});
            skLineSegment(sketch, "E6.3.3.2", {"start": v(-139.7, 2314.57) * mm, "end": v(-292.1, 2314.57) * mm});
            skLineSegment(sketch, "E6.6.3.2", {"start": v(-136.52, 2314.57) * mm, "end": v(-136.52, 2466.97) * mm});
            skLineSegment(sketch, "E6.9.3.2", {"start": v(15.88, 2470.15) * mm, "end": v(-136.52, 2470.15) * mm});
            skLineSegment(sketch, "E6.12.3.2", {"start": v(-136.52, 2314.57) * mm, "end": v(473.08, 2314.57) * mm});
            skLineSegment(sketch, "E6.15.3.2", {"start": v(-139.7, 2314.57) * mm, "end": v(-139.7, 2924.17) * mm});
            skLineSegment(sketch, "E6.18.3.2", {"start": v(-136.52, 2466.97) * mm, "end": v(473.08, 2466.97) * mm});
            skLineSegment(sketch, "E6.21.3.2", {"start": v(15.88, 3079.75) * mm, "end": v(-136.52, 3079.75) * mm});
            skLineSegment(sketch, "E6.24.3.2", {"start": v(-292.1, 2314.57) * mm, "end": v(-292.1, 2924.17) * mm});
            skLineSegment(sketch, "E6.27.3.2", {"start": v(-136.52, 2470.15) * mm, "end": v(-136.52, 3079.75) * mm});
            skLineSegment(sketch, "E6.30.3.2", {"start": v(317.5, 2159) * mm, "end": v(317.5, 2311.4) * mm});
            skLineSegment(sketch, "E6.33.3.2", {"start": v(15.88, 2470.15) * mm, "end": v(15.88, 3079.75) * mm});
            skLineSegment(sketch, "E6.36.3.2", {"start": v(-292.1, 2159) * mm, "end": v(-292.1, 2311.4) * mm});
            skLineSegment(sketch, "E6.39.3.2", {"start": v(-139.7, 2924.17) * mm, "end": v(-292.1, 2924.17) * mm});
            skLineSegment(sketch, "E6.42.3.2", {"start": v(473.08, 2314.57) * mm, "end": v(473.08, 2466.97) * mm});
            skLineSegment(sketch, "E6.45.3.2", {"start": v(-292.1, 2311.4) * mm, "end": v(317.5, 2311.4) * mm});
            skLineSegment(sketch, "E6.0.3.3", {"start": v(-904.87, 2771.77) * mm, "end": v(-295.27, 2771.77) * mm});
            skLineSegment(sketch, "E6.3.3.3", {"start": v(-752.47, 2927.35) * mm, "end": v(-904.87, 2927.35) * mm});
            skLineSegment(sketch, "E6.6.3.3", {"start": v(-749.3, 2927.35) * mm, "end": v(-749.3, 3079.75) * mm});
            skLineSegment(sketch, "E6.9.3.3", {"start": v(-596.9, 3082.92) * mm, "end": v(-749.3, 3082.92) * mm});
            skLineSegment(sketch, "E6.12.3.3", {"start": v(-749.3, 2927.35) * mm, "end": v(-139.7, 2927.35) * mm});
            skLineSegment(sketch, "E6.15.3.3", {"start": v(-752.47, 2927.35) * mm, "end": v(-752.47, 3536.95) * mm});
            skLineSegment(sketch, "E6.18.3.3", {"start": v(-749.3, 3079.75) * mm, "end": v(-139.7, 3079.75) * mm});
            skLineSegment(sketch, "E6.21.3.3", {"start": v(-596.9, 3692.52) * mm, "end": v(-749.3, 3692.52) * mm});
            skLineSegment(sketch, "E6.24.3.3", {"start": v(-904.87, 2927.35) * mm, "end": v(-904.87, 3536.95) * mm});
            skLineSegment(sketch, "E6.27.3.3", {"start": v(-749.3, 3082.92) * mm, "end": v(-749.3, 3692.52) * mm});
            skLineSegment(sketch, "E6.30.3.3", {"start": v(-295.27, 2771.77) * mm, "end": v(-295.27, 2924.17) * mm});
            skLineSegment(sketch, "E6.33.3.3", {"start": v(-596.9, 3082.92) * mm, "end": v(-596.9, 3692.52) * mm});
            skLineSegment(sketch, "E6.36.3.3", {"start": v(-904.87, 2771.77) * mm, "end": v(-904.87, 2924.17) * mm});
            skLineSegment(sketch, "E6.39.3.3", {"start": v(-752.47, 3536.95) * mm, "end": v(-904.87, 3536.95) * mm});
            skLineSegment(sketch, "E6.42.3.3", {"start": v(-139.7, 2927.35) * mm, "end": v(-139.7, 3079.75) * mm});
            skLineSegment(sketch, "E6.45.3.3", {"start": v(-904.87, 2924.17) * mm, "end": v(-295.27, 2924.17) * mm});
            skLineSegment(sketch, "E6.0.3.4", {"start": v(-1517.65, 3384.55) * mm, "end": v(-908.05, 3384.55) * mm});
            skLineSegment(sketch, "E6.3.3.4", {"start": v(-1365.25, 3540.12) * mm, "end": v(-1517.65, 3540.12) * mm});
            skLineSegment(sketch, "E6.6.3.4", {"start": v(-1362.07, 3540.12) * mm, "end": v(-1362.07, 3692.52) * mm});
            skLineSegment(sketch, "E6.9.3.4", {"start": v(-1209.67, 3695.7) * mm, "end": v(-1362.07, 3695.7) * mm});
            skLineSegment(sketch, "E6.12.3.4", {"start": v(-1362.07, 3540.12) * mm, "end": v(-752.47, 3540.12) * mm});
            skLineSegment(sketch, "E6.15.3.4", {"start": v(-1365.25, 3540.12) * mm, "end": v(-1365.25, 4149.72) * mm});
            skLineSegment(sketch, "E6.18.3.4", {"start": v(-1362.07, 3692.52) * mm, "end": v(-752.47, 3692.52) * mm});
            skLineSegment(sketch, "E6.21.3.4", {"start": v(-1209.67, 4305.3) * mm, "end": v(-1362.07, 4305.3) * mm});
            skLineSegment(sketch, "E6.24.3.4", {"start": v(-1517.65, 3540.12) * mm, "end": v(-1517.65, 4149.72) * mm});
            skLineSegment(sketch, "E6.27.3.4", {"start": v(-1362.07, 3695.7) * mm, "end": v(-1362.07, 4305.3) * mm});
            skLineSegment(sketch, "E6.30.3.4", {"start": v(-908.05, 3384.55) * mm, "end": v(-908.05, 3536.95) * mm});
            skLineSegment(sketch, "E6.33.3.4", {"start": v(-1209.67, 3695.7) * mm, "end": v(-1209.67, 4305.3) * mm});
            skLineSegment(sketch, "E6.36.3.4", {"start": v(-1517.65, 3384.55) * mm, "end": v(-1517.65, 3536.95) * mm});
            skLineSegment(sketch, "E6.39.3.4", {"start": v(-1365.25, 4149.72) * mm, "end": v(-1517.65, 4149.72) * mm});
            skLineSegment(sketch, "E6.42.3.4", {"start": v(-752.47, 3540.12) * mm, "end": v(-752.47, 3692.52) * mm});
            skLineSegment(sketch, "E6.45.3.4", {"start": v(-1517.65, 3536.95) * mm, "end": v(-908.05, 3536.95) * mm});
            skLineSegment(sketch, "E6.0.4.2", {"start": v(19.05, 2470.15) * mm, "end": v(628.65, 2470.15) * mm});
            skLineSegment(sketch, "E6.3.4.2", {"start": v(171.45, 2625.72) * mm, "end": v(19.05, 2625.72) * mm});
            skLineSegment(sketch, "E6.6.4.2", {"start": v(174.63, 2625.72) * mm, "end": v(174.63, 2778.12) * mm});
            skLineSegment(sketch, "E6.9.4.2", {"start": v(327.03, 2781.3) * mm, "end": v(174.63, 2781.3) * mm});
            skLineSegment(sketch, "E6.12.4.2", {"start": v(174.63, 2625.72) * mm, "end": v(784.23, 2625.72) * mm});
            skLineSegment(sketch, "E6.15.4.2", {"start": v(171.45, 2625.72) * mm, "end": v(171.45, 3235.32) * mm});
            skLineSegment(sketch, "E6.18.4.2", {"start": v(174.63, 2778.12) * mm, "end": v(784.23, 2778.12) * mm});
            skLineSegment(sketch, "E6.21.4.2", {"start": v(327.03, 3390.9) * mm, "end": v(174.63, 3390.9) * mm});
            skLineSegment(sketch, "E6.24.4.2", {"start": v(19.05, 2625.72) * mm, "end": v(19.05, 3235.32) * mm});
            skLineSegment(sketch, "E6.27.4.2", {"start": v(174.63, 2781.3) * mm, "end": v(174.63, 3390.9) * mm});
            skLineSegment(sketch, "E6.30.4.2", {"start": v(628.65, 2470.15) * mm, "end": v(628.65, 2622.55) * mm});
            skLineSegment(sketch, "E6.33.4.2", {"start": v(327.03, 2781.3) * mm, "end": v(327.03, 3390.9) * mm});
            skLineSegment(sketch, "E6.36.4.2", {"start": v(19.05, 2470.15) * mm, "end": v(19.05, 2622.55) * mm});
            skLineSegment(sketch, "E6.39.4.2", {"start": v(171.45, 3235.32) * mm, "end": v(19.05, 3235.32) * mm});
            skLineSegment(sketch, "E6.42.4.2", {"start": v(784.23, 2625.72) * mm, "end": v(784.23, 2778.12) * mm});
            skLineSegment(sketch, "E6.45.4.2", {"start": v(19.05, 2622.55) * mm, "end": v(628.65, 2622.55) * mm});
            skLineSegment(sketch, "E6.0.4.3", {"start": v(-593.72, 3082.92) * mm, "end": v(15.88, 3082.92) * mm});
            skLineSegment(sketch, "E6.3.4.3", {"start": v(-441.32, 3238.5) * mm, "end": v(-593.72, 3238.5) * mm});
            skLineSegment(sketch, "E6.6.4.3", {"start": v(-438.15, 3238.5) * mm, "end": v(-438.15, 3390.9) * mm});
            skLineSegment(sketch, "E6.9.4.3", {"start": v(-285.75, 3394.07) * mm, "end": v(-438.15, 3394.07) * mm});
            skLineSegment(sketch, "E6.12.4.3", {"start": v(-438.15, 3238.5) * mm, "end": v(171.45, 3238.5) * mm});
            skLineSegment(sketch, "E6.15.4.3", {"start": v(-441.32, 3238.5) * mm, "end": v(-441.32, 3848.1) * mm});
            skLineSegment(sketch, "E6.18.4.3", {"start": v(-438.15, 3390.9) * mm, "end": v(171.45, 3390.9) * mm});
            skLineSegment(sketch, "E6.21.4.3", {"start": v(-285.75, 4003.67) * mm, "end": v(-438.15, 4003.67) * mm});
            skLineSegment(sketch, "E6.24.4.3", {"start": v(-593.72, 3238.5) * mm, "end": v(-593.72, 3848.1) * mm});
            skLineSegment(sketch, "E6.27.4.3", {"start": v(-438.15, 3394.07) * mm, "end": v(-438.15, 4003.67) * mm});
            skLineSegment(sketch, "E6.30.4.3", {"start": v(15.88, 3082.92) * mm, "end": v(15.88, 3235.32) * mm});
            skLineSegment(sketch, "E6.33.4.3", {"start": v(-285.75, 3394.07) * mm, "end": v(-285.75, 4003.67) * mm});
            skLineSegment(sketch, "E6.36.4.3", {"start": v(-593.72, 3082.92) * mm, "end": v(-593.72, 3235.32) * mm});
            skLineSegment(sketch, "E6.39.4.3", {"start": v(-441.32, 3848.1) * mm, "end": v(-593.72, 3848.1) * mm});
            skLineSegment(sketch, "E6.42.4.3", {"start": v(171.45, 3238.5) * mm, "end": v(171.45, 3390.9) * mm});
            skLineSegment(sketch, "E6.45.4.3", {"start": v(-593.72, 3235.32) * mm, "end": v(15.88, 3235.32) * mm});
            skLineSegment(sketch, "E6.0.4.4", {"start": v(-1206.5, 3695.7) * mm, "end": v(-596.9, 3695.7) * mm});
            skLineSegment(sketch, "E6.3.4.4", {"start": v(-1054.1, 3851.27) * mm, "end": v(-1206.5, 3851.27) * mm});
            skLineSegment(sketch, "E6.6.4.4", {"start": v(-1050.92, 3851.27) * mm, "end": v(-1050.92, 4003.67) * mm});
            skLineSegment(sketch, "E6.9.4.4", {"start": v(-898.52, 4006.85) * mm, "end": v(-1050.92, 4006.85) * mm});
            skLineSegment(sketch, "E6.12.4.4", {"start": v(-1050.92, 3851.27) * mm, "end": v(-441.32, 3851.27) * mm});
            skLineSegment(sketch, "E6.15.4.4", {"start": v(-1054.1, 3851.27) * mm, "end": v(-1054.1, 4460.87) * mm});
            skLineSegment(sketch, "E6.18.4.4", {"start": v(-1050.92, 4003.67) * mm, "end": v(-441.32, 4003.67) * mm});
            skLineSegment(sketch, "E6.21.4.4", {"start": v(-898.52, 4616.45) * mm, "end": v(-1050.92, 4616.45) * mm});
            skLineSegment(sketch, "E6.24.4.4", {"start": v(-1206.5, 3851.27) * mm, "end": v(-1206.5, 4460.87) * mm});
            skLineSegment(sketch, "E6.27.4.4", {"start": v(-1050.92, 4006.85) * mm, "end": v(-1050.92, 4616.45) * mm});
            skLineSegment(sketch, "E6.30.4.4", {"start": v(-596.9, 3695.7) * mm, "end": v(-596.9, 3848.1) * mm});
            skLineSegment(sketch, "E6.33.4.4", {"start": v(-898.52, 4006.85) * mm, "end": v(-898.52, 4616.45) * mm});
            skLineSegment(sketch, "E6.36.4.4", {"start": v(-1206.5, 3695.7) * mm, "end": v(-1206.5, 3848.1) * mm});
            skLineSegment(sketch, "E6.39.4.4", {"start": v(-1054.1, 4460.87) * mm, "end": v(-1206.5, 4460.87) * mm});
            skLineSegment(sketch, "E6.42.4.4", {"start": v(-441.32, 3851.27) * mm, "end": v(-441.32, 4003.67) * mm});
            skLineSegment(sketch, "E6.45.4.4", {"start": v(-1206.5, 3848.1) * mm, "end": v(-596.9, 3848.1) * mm});
            skLineSegment(sketch, "E6.0.5.2", {"start": v(330.2, 2781.3) * mm, "end": v(939.8, 2781.3) * mm});
            skLineSegment(sketch, "E6.3.5.2", {"start": v(482.6, 2936.87) * mm, "end": v(330.2, 2936.87) * mm});
            skLineSegment(sketch, "E6.6.5.2", {"start": v(485.78, 2936.87) * mm, "end": v(485.78, 3089.27) * mm});
            skLineSegment(sketch, "E6.9.5.2", {"start": v(638.18, 3092.45) * mm, "end": v(485.78, 3092.45) * mm});
            skLineSegment(sketch, "E6.12.5.2", {"start": v(485.78, 2936.87) * mm, "end": v(1095.38, 2936.87) * mm});
            skLineSegment(sketch, "E6.15.5.2", {"start": v(482.6, 2936.87) * mm, "end": v(482.6, 3546.47) * mm});
            skLineSegment(sketch, "E6.18.5.2", {"start": v(485.78, 3089.27) * mm, "end": v(1095.38, 3089.27) * mm});
            skLineSegment(sketch, "E6.21.5.2", {"start": v(638.18, 3702.05) * mm, "end": v(485.78, 3702.05) * mm});
            skLineSegment(sketch, "E6.24.5.2", {"start": v(330.2, 2936.87) * mm, "end": v(330.2, 3546.47) * mm});
            skLineSegment(sketch, "E6.27.5.2", {"start": v(485.78, 3092.45) * mm, "end": v(485.78, 3702.05) * mm});
            skLineSegment(sketch, "E6.30.5.2", {"start": v(939.8, 2781.3) * mm, "end": v(939.8, 2933.7) * mm});
            skLineSegment(sketch, "E6.33.5.2", {"start": v(638.18, 3092.45) * mm, "end": v(638.18, 3702.05) * mm});
            skLineSegment(sketch, "E6.36.5.2", {"start": v(330.2, 2781.3) * mm, "end": v(330.2, 2933.7) * mm});
            skLineSegment(sketch, "E6.39.5.2", {"start": v(482.6, 3546.47) * mm, "end": v(330.2, 3546.47) * mm});
            skLineSegment(sketch, "E6.42.5.2", {"start": v(1095.38, 2936.87) * mm, "end": v(1095.38, 3089.27) * mm});
            skLineSegment(sketch, "E6.45.5.2", {"start": v(330.2, 2933.7) * mm, "end": v(939.8, 2933.7) * mm});
            skLineSegment(sketch, "E6.0.5.3", {"start": v(-282.57, 3394.07) * mm, "end": v(327.03, 3394.07) * mm});
            skLineSegment(sketch, "E6.3.5.3", {"start": v(-130.17, 3549.65) * mm, "end": v(-282.57, 3549.65) * mm});
            skLineSegment(sketch, "E6.6.5.3", {"start": v(-127, 3549.65) * mm, "end": v(-127, 3702.05) * mm});
            skLineSegment(sketch, "E6.9.5.3", {"start": v(25.4, 3705.22) * mm, "end": v(-127, 3705.22) * mm});
            skLineSegment(sketch, "E6.12.5.3", {"start": v(-127, 3549.65) * mm, "end": v(482.6, 3549.65) * mm});
            skLineSegment(sketch, "E6.15.5.3", {"start": v(-130.17, 3549.65) * mm, "end": v(-130.17, 4159.25) * mm});
            skLineSegment(sketch, "E6.18.5.3", {"start": v(-127, 3702.05) * mm, "end": v(482.6, 3702.05) * mm});
            skLineSegment(sketch, "E6.21.5.3", {"start": v(25.4, 4314.82) * mm, "end": v(-127, 4314.82) * mm});
            skLineSegment(sketch, "E6.24.5.3", {"start": v(-282.57, 3549.65) * mm, "end": v(-282.57, 4159.25) * mm});
            skLineSegment(sketch, "E6.27.5.3", {"start": v(-127, 3705.22) * mm, "end": v(-127, 4314.82) * mm});
            skLineSegment(sketch, "E6.30.5.3", {"start": v(327.03, 3394.07) * mm, "end": v(327.03, 3546.47) * mm});
            skLineSegment(sketch, "E6.33.5.3", {"start": v(25.4, 3705.22) * mm, "end": v(25.4, 4314.82) * mm});
            skLineSegment(sketch, "E6.36.5.3", {"start": v(-282.57, 3394.07) * mm, "end": v(-282.57, 3546.47) * mm});
            skLineSegment(sketch, "E6.39.5.3", {"start": v(-130.17, 4159.25) * mm, "end": v(-282.57, 4159.25) * mm});
            skLineSegment(sketch, "E6.42.5.3", {"start": v(482.6, 3549.65) * mm, "end": v(482.6, 3702.05) * mm});
            skLineSegment(sketch, "E6.45.5.3", {"start": v(-282.57, 3546.47) * mm, "end": v(327.03, 3546.47) * mm});
            skLineSegment(sketch, "E6.0.5.4", {"start": v(-895.35, 4006.85) * mm, "end": v(-285.75, 4006.85) * mm});
            skLineSegment(sketch, "E6.3.5.4", {"start": v(-742.95, 4162.42) * mm, "end": v(-895.35, 4162.42) * mm});
            skLineSegment(sketch, "E6.6.5.4", {"start": v(-739.77, 4162.42) * mm, "end": v(-739.77, 4314.82) * mm});
            skLineSegment(sketch, "E6.9.5.4", {"start": v(-587.37, 4318) * mm, "end": v(-739.77, 4318) * mm});
            skLineSegment(sketch, "E6.12.5.4", {"start": v(-739.77, 4162.42) * mm, "end": v(-130.17, 4162.42) * mm});
            skLineSegment(sketch, "E6.15.5.4", {"start": v(-742.95, 4162.42) * mm, "end": v(-742.95, 4772.02) * mm});
            skLineSegment(sketch, "E6.18.5.4", {"start": v(-739.77, 4314.82) * mm, "end": v(-130.17, 4314.82) * mm});
            skLineSegment(sketch, "E6.21.5.4", {"start": v(-587.37, 4927.6) * mm, "end": v(-739.77, 4927.6) * mm});
            skLineSegment(sketch, "E6.24.5.4", {"start": v(-895.35, 4162.42) * mm, "end": v(-895.35, 4772.02) * mm});
            skLineSegment(sketch, "E6.27.5.4", {"start": v(-739.77, 4318) * mm, "end": v(-739.77, 4927.6) * mm});
            skLineSegment(sketch, "E6.30.5.4", {"start": v(-285.75, 4006.85) * mm, "end": v(-285.75, 4159.25) * mm});
            skLineSegment(sketch, "E6.33.5.4", {"start": v(-587.37, 4318) * mm, "end": v(-587.37, 4927.6) * mm});
            skLineSegment(sketch, "E6.36.5.4", {"start": v(-895.35, 4006.85) * mm, "end": v(-895.35, 4159.25) * mm});
            skLineSegment(sketch, "E6.39.5.4", {"start": v(-742.95, 4772.02) * mm, "end": v(-895.35, 4772.02) * mm});
            skLineSegment(sketch, "E6.42.5.4", {"start": v(-130.17, 4162.42) * mm, "end": v(-130.17, 4314.82) * mm});
            skLineSegment(sketch, "E6.45.5.4", {"start": v(-895.35, 4159.25) * mm, "end": v(-285.75, 4159.25) * mm});
            skLineSegment(sketch, "E7.0.6.0", {"start": v(1866.9, 1866.9) * mm, "end": v(2476.5, 1866.9) * mm});
            skLineSegment(sketch, "E7.3.6.0", {"start": v(2019.3, 2022.47) * mm, "end": v(1866.9, 2022.47) * mm});
            skLineSegment(sketch, "E7.6.6.0", {"start": v(2022.48, 2022.47) * mm, "end": v(2022.48, 2174.87) * mm});
            skLineSegment(sketch, "E7.9.6.0", {"start": v(2174.88, 2178.05) * mm, "end": v(2022.48, 2178.05) * mm});
            skLineSegment(sketch, "E7.12.6.0", {"start": v(2022.48, 2022.47) * mm, "end": v(2632.08, 2022.47) * mm});
            skLineSegment(sketch, "E7.15.6.0", {"start": v(2019.3, 2022.47) * mm, "end": v(2019.3, 2632.07) * mm});
            skLineSegment(sketch, "E7.18.6.0", {"start": v(2022.48, 2174.87) * mm, "end": v(2632.08, 2174.87) * mm});
            skLineSegment(sketch, "E7.21.6.0", {"start": v(2174.88, 2787.65) * mm, "end": v(2022.48, 2787.65) * mm});
            skLineSegment(sketch, "E7.24.6.0", {"start": v(1866.9, 2022.47) * mm, "end": v(1866.9, 2632.07) * mm});
            skLineSegment(sketch, "E7.27.6.0", {"start": v(2022.48, 2178.05) * mm, "end": v(2022.48, 2787.65) * mm});
            skLineSegment(sketch, "E7.30.6.0", {"start": v(2476.5, 1866.9) * mm, "end": v(2476.5, 2019.3) * mm});
            skLineSegment(sketch, "E7.33.6.0", {"start": v(2174.88, 2178.05) * mm, "end": v(2174.88, 2787.65) * mm});
            skLineSegment(sketch, "E7.36.6.0", {"start": v(1866.9, 1866.9) * mm, "end": v(1866.9, 2019.3) * mm});
            skLineSegment(sketch, "E7.39.6.0", {"start": v(2019.3, 2632.07) * mm, "end": v(1866.9, 2632.07) * mm});
            skLineSegment(sketch, "E7.42.6.0", {"start": v(2632.08, 2022.47) * mm, "end": v(2632.08, 2174.87) * mm});
            skLineSegment(sketch, "E7.45.6.0", {"start": v(1866.9, 2019.3) * mm, "end": v(2476.5, 2019.3) * mm});
            skLineSegment(sketch, "E7.0.6.1", {"start": v(1254.13, 2479.67) * mm, "end": v(1863.73, 2479.67) * mm});
            skLineSegment(sketch, "E7.3.6.1", {"start": v(1406.53, 2635.25) * mm, "end": v(1254.13, 2635.25) * mm});
            skLineSegment(sketch, "E7.6.6.1", {"start": v(1409.7, 2635.25) * mm, "end": v(1409.7, 2787.65) * mm});
            skLineSegment(sketch, "E7.9.6.1", {"start": v(1562.1, 2790.82) * mm, "end": v(1409.7, 2790.82) * mm});
            skLineSegment(sketch, "E7.12.6.1", {"start": v(1409.7, 2635.25) * mm, "end": v(2019.3, 2635.25) * mm});
            skLineSegment(sketch, "E7.15.6.1", {"start": v(1406.53, 2635.25) * mm, "end": v(1406.53, 3244.85) * mm});
            skLineSegment(sketch, "E7.18.6.1", {"start": v(1409.7, 2787.65) * mm, "end": v(2019.3, 2787.65) * mm});
            skLineSegment(sketch, "E7.21.6.1", {"start": v(1562.1, 3400.42) * mm, "end": v(1409.7, 3400.42) * mm});
            skLineSegment(sketch, "E7.24.6.1", {"start": v(1254.13, 2635.25) * mm, "end": v(1254.13, 3244.85) * mm});
            skLineSegment(sketch, "E7.27.6.1", {"start": v(1409.7, 2790.82) * mm, "end": v(1409.7, 3400.42) * mm});
            skLineSegment(sketch, "E7.30.6.1", {"start": v(1863.73, 2479.67) * mm, "end": v(1863.73, 2632.07) * mm});
            skLineSegment(sketch, "E7.33.6.1", {"start": v(1562.1, 2790.82) * mm, "end": v(1562.1, 3400.42) * mm});
            skLineSegment(sketch, "E7.36.6.1", {"start": v(1254.13, 2479.67) * mm, "end": v(1254.13, 2632.07) * mm});
            skLineSegment(sketch, "E7.39.6.1", {"start": v(1406.53, 3244.85) * mm, "end": v(1254.13, 3244.85) * mm});
            skLineSegment(sketch, "E7.42.6.1", {"start": v(2019.3, 2635.25) * mm, "end": v(2019.3, 2787.65) * mm});
            skLineSegment(sketch, "E7.45.6.1", {"start": v(1254.13, 2632.07) * mm, "end": v(1863.73, 2632.07) * mm});
            skLineSegment(sketch, "E7.0.6.2", {"start": v(641.35, 3092.45) * mm, "end": v(1250.95, 3092.45) * mm});
            skLineSegment(sketch, "E7.3.6.2", {"start": v(793.75, 3248.02) * mm, "end": v(641.35, 3248.02) * mm});
            skLineSegment(sketch, "E7.6.6.2", {"start": v(796.92, 3248.02) * mm, "end": v(796.92, 3400.42) * mm});
            skLineSegment(sketch, "E7.9.6.2", {"start": v(949.32, 3403.6) * mm, "end": v(796.92, 3403.6) * mm});
            skLineSegment(sketch, "E7.12.6.2", {"start": v(796.92, 3248.02) * mm, "end": v(1406.52, 3248.02) * mm});
            skLineSegment(sketch, "E7.15.6.2", {"start": v(793.75, 3248.02) * mm, "end": v(793.75, 3857.62) * mm});
            skLineSegment(sketch, "E7.18.6.2", {"start": v(796.92, 3400.42) * mm, "end": v(1406.52, 3400.42) * mm});
            skLineSegment(sketch, "E7.21.6.2", {"start": v(949.32, 4013.2) * mm, "end": v(796.92, 4013.2) * mm});
            skLineSegment(sketch, "E7.24.6.2", {"start": v(641.35, 3248.02) * mm, "end": v(641.35, 3857.62) * mm});
            skLineSegment(sketch, "E7.27.6.2", {"start": v(796.92, 3403.6) * mm, "end": v(796.92, 4013.2) * mm});
            skLineSegment(sketch, "E7.30.6.2", {"start": v(1250.95, 3092.45) * mm, "end": v(1250.95, 3244.85) * mm});
            skLineSegment(sketch, "E7.33.6.2", {"start": v(949.32, 3403.6) * mm, "end": v(949.32, 4013.2) * mm});
            skLineSegment(sketch, "E7.36.6.2", {"start": v(641.35, 3092.45) * mm, "end": v(641.35, 3244.85) * mm});
            skLineSegment(sketch, "E7.39.6.2", {"start": v(793.75, 3857.62) * mm, "end": v(641.35, 3857.62) * mm});
            skLineSegment(sketch, "E7.42.6.2", {"start": v(1406.52, 3248.02) * mm, "end": v(1406.52, 3400.42) * mm});
            skLineSegment(sketch, "E7.45.6.2", {"start": v(641.35, 3244.85) * mm, "end": v(1250.95, 3244.85) * mm});
            skLineSegment(sketch, "E7.0.6.3", {"start": v(28.57, 3705.22) * mm, "end": v(638.17, 3705.22) * mm});
            skLineSegment(sketch, "E7.3.6.3", {"start": v(180.97, 3860.8) * mm, "end": v(28.57, 3860.8) * mm});
            skLineSegment(sketch, "E7.6.6.3", {"start": v(184.15, 3860.8) * mm, "end": v(184.15, 4013.2) * mm});
            skLineSegment(sketch, "E7.9.6.3", {"start": v(336.55, 4016.37) * mm, "end": v(184.15, 4016.37) * mm});
            skLineSegment(sketch, "E7.12.6.3", {"start": v(184.15, 3860.8) * mm, "end": v(793.75, 3860.8) * mm});
            skLineSegment(sketch, "E7.15.6.3", {"start": v(180.97, 3860.8) * mm, "end": v(180.97, 4470.4) * mm});
            skLineSegment(sketch, "E7.18.6.3", {"start": v(184.15, 4013.2) * mm, "end": v(793.75, 4013.2) * mm});
            skLineSegment(sketch, "E7.21.6.3", {"start": v(336.55, 4625.97) * mm, "end": v(184.15, 4625.97) * mm});
            skLineSegment(sketch, "E7.24.6.3", {"start": v(28.57, 3860.8) * mm, "end": v(28.57, 4470.4) * mm});
            skLineSegment(sketch, "E7.27.6.3", {"start": v(184.15, 4016.37) * mm, "end": v(184.15, 4625.97) * mm});
            skLineSegment(sketch, "E7.30.6.3", {"start": v(638.17, 3705.22) * mm, "end": v(638.17, 3857.62) * mm});
            skLineSegment(sketch, "E7.33.6.3", {"start": v(336.55, 4016.37) * mm, "end": v(336.55, 4625.97) * mm});
            skLineSegment(sketch, "E7.36.6.3", {"start": v(28.57, 3705.22) * mm, "end": v(28.57, 3857.62) * mm});
            skLineSegment(sketch, "E7.39.6.3", {"start": v(180.97, 4470.4) * mm, "end": v(28.57, 4470.4) * mm});
            skLineSegment(sketch, "E7.42.6.3", {"start": v(793.75, 3860.8) * mm, "end": v(793.75, 4013.2) * mm});
            skLineSegment(sketch, "E7.45.6.3", {"start": v(28.57, 3857.62) * mm, "end": v(638.17, 3857.62) * mm});
            skLineSegment(sketch, "E7.0.6.4", {"start": v(-584.2, 4318) * mm, "end": v(25.4, 4318) * mm});
            skLineSegment(sketch, "E7.3.6.4", {"start": v(-431.8, 4473.57) * mm, "end": v(-584.2, 4473.57) * mm});
            skLineSegment(sketch, "E7.6.6.4", {"start": v(-428.63, 4473.57) * mm, "end": v(-428.63, 4625.97) * mm});
            skLineSegment(sketch, "E7.9.6.4", {"start": v(-276.23, 4629.15) * mm, "end": v(-428.63, 4629.15) * mm});
            skLineSegment(sketch, "E7.12.6.4", {"start": v(-428.63, 4473.57) * mm, "end": v(180.97, 4473.57) * mm});
            skLineSegment(sketch, "E7.15.6.4", {"start": v(-431.8, 4473.57) * mm, "end": v(-431.8, 5083.18) * mm});
            skLineSegment(sketch, "E7.18.6.4", {"start": v(-428.63, 4625.97) * mm, "end": v(180.97, 4625.97) * mm});
            skLineSegment(sketch, "E7.21.6.4", {"start": v(-276.23, 5238.75) * mm, "end": v(-428.63, 5238.75) * mm});
            skLineSegment(sketch, "E7.24.6.4", {"start": v(-584.2, 4473.57) * mm, "end": v(-584.2, 5083.18) * mm});
            skLineSegment(sketch, "E7.27.6.4", {"start": v(-428.63, 4629.15) * mm, "end": v(-428.63, 5238.75) * mm});
            skLineSegment(sketch, "E7.30.6.4", {"start": v(25.4, 4318) * mm, "end": v(25.4, 4470.4) * mm});
            skLineSegment(sketch, "E7.33.6.4", {"start": v(-276.23, 4629.15) * mm, "end": v(-276.23, 5238.75) * mm});
            skLineSegment(sketch, "E7.36.6.4", {"start": v(-584.2, 4318) * mm, "end": v(-584.2, 4470.4) * mm});
            skLineSegment(sketch, "E7.39.6.4", {"start": v(-431.8, 5083.18) * mm, "end": v(-584.2, 5083.18) * mm});
            skLineSegment(sketch, "E7.42.6.4", {"start": v(180.97, 4473.57) * mm, "end": v(180.97, 4625.97) * mm});
            skLineSegment(sketch, "E7.45.6.4", {"start": v(-584.2, 4470.4) * mm, "end": v(25.4, 4470.4) * mm});
            skLineSegment(sketch, "E7.0.7.0", {"start": v(2178.05, 2178.05) * mm, "end": v(2787.65, 2178.05) * mm});
            skLineSegment(sketch, "E7.3.7.0", {"start": v(2330.45, 2333.62) * mm, "end": v(2178.05, 2333.62) * mm});
            skLineSegment(sketch, "E7.6.7.0", {"start": v(2333.63, 2333.62) * mm, "end": v(2333.63, 2486.02) * mm});
            skLineSegment(sketch, "E7.9.7.0", {"start": v(2486.03, 2489.2) * mm, "end": v(2333.63, 2489.2) * mm});
            skLineSegment(sketch, "E7.12.7.0", {"start": v(2333.63, 2333.62) * mm, "end": v(2943.23, 2333.62) * mm});
            skLineSegment(sketch, "E7.15.7.0", {"start": v(2330.45, 2333.62) * mm, "end": v(2330.45, 2943.22) * mm});
            skLineSegment(sketch, "E7.18.7.0", {"start": v(2333.63, 2486.02) * mm, "end": v(2943.23, 2486.02) * mm});
            skLineSegment(sketch, "E7.21.7.0", {"start": v(2486.03, 3098.8) * mm, "end": v(2333.63, 3098.8) * mm});
            skLineSegment(sketch, "E7.24.7.0", {"start": v(2178.05, 2333.62) * mm, "end": v(2178.05, 2943.22) * mm});
            skLineSegment(sketch, "E7.27.7.0", {"start": v(2333.63, 2489.2) * mm, "end": v(2333.63, 3098.8) * mm});
            skLineSegment(sketch, "E7.30.7.0", {"start": v(2787.65, 2178.05) * mm, "end": v(2787.65, 2330.45) * mm});
            skLineSegment(sketch, "E7.33.7.0", {"start": v(2486.03, 2489.2) * mm, "end": v(2486.03, 3098.8) * mm});
            skLineSegment(sketch, "E7.36.7.0", {"start": v(2178.05, 2178.05) * mm, "end": v(2178.05, 2330.45) * mm});
            skLineSegment(sketch, "E7.39.7.0", {"start": v(2330.45, 2943.22) * mm, "end": v(2178.05, 2943.22) * mm});
            skLineSegment(sketch, "E7.42.7.0", {"start": v(2943.23, 2333.62) * mm, "end": v(2943.23, 2486.02) * mm});
            skLineSegment(sketch, "E7.45.7.0", {"start": v(2178.05, 2330.45) * mm, "end": v(2787.65, 2330.45) * mm});
            skLineSegment(sketch, "E7.0.7.1", {"start": v(1565.28, 2790.82) * mm, "end": v(2174.88, 2790.82) * mm});
            skLineSegment(sketch, "E7.3.7.1", {"start": v(1717.68, 2946.4) * mm, "end": v(1565.28, 2946.4) * mm});
            skLineSegment(sketch, "E7.6.7.1", {"start": v(1720.85, 2946.4) * mm, "end": v(1720.85, 3098.8) * mm});
            skLineSegment(sketch, "E7.9.7.1", {"start": v(1873.25, 3101.97) * mm, "end": v(1720.85, 3101.97) * mm});
            skLineSegment(sketch, "E7.12.7.1", {"start": v(1720.85, 2946.4) * mm, "end": v(2330.45, 2946.4) * mm});
            skLineSegment(sketch, "E7.15.7.1", {"start": v(1717.68, 2946.4) * mm, "end": v(1717.68, 3556) * mm});
            skLineSegment(sketch, "E7.18.7.1", {"start": v(1720.85, 3098.8) * mm, "end": v(2330.45, 3098.8) * mm});
            skLineSegment(sketch, "E7.21.7.1", {"start": v(1873.25, 3711.57) * mm, "end": v(1720.85, 3711.57) * mm});
            skLineSegment(sketch, "E7.24.7.1", {"start": v(1565.28, 2946.4) * mm, "end": v(1565.28, 3556) * mm});
            skLineSegment(sketch, "E7.27.7.1", {"start": v(1720.85, 3101.97) * mm, "end": v(1720.85, 3711.57) * mm});
            skLineSegment(sketch, "E7.30.7.1", {"start": v(2174.88, 2790.82) * mm, "end": v(2174.88, 2943.22) * mm});
            skLineSegment(sketch, "E7.33.7.1", {"start": v(1873.25, 3101.97) * mm, "end": v(1873.25, 3711.57) * mm});
            skLineSegment(sketch, "E7.36.7.1", {"start": v(1565.28, 2790.82) * mm, "end": v(1565.28, 2943.22) * mm});
            skLineSegment(sketch, "E7.39.7.1", {"start": v(1717.68, 3556) * mm, "end": v(1565.28, 3556) * mm});
            skLineSegment(sketch, "E7.42.7.1", {"start": v(2330.45, 2946.4) * mm, "end": v(2330.45, 3098.8) * mm});
            skLineSegment(sketch, "E7.45.7.1", {"start": v(1565.28, 2943.22) * mm, "end": v(2174.88, 2943.22) * mm});
            skLineSegment(sketch, "E7.0.7.2", {"start": v(952.5, 3403.6) * mm, "end": v(1562.1, 3403.6) * mm});
            skLineSegment(sketch, "E7.3.7.2", {"start": v(1104.9, 3559.17) * mm, "end": v(952.5, 3559.17) * mm});
            skLineSegment(sketch, "E7.6.7.2", {"start": v(1108.07, 3559.17) * mm, "end": v(1108.07, 3711.57) * mm});
            skLineSegment(sketch, "E7.9.7.2", {"start": v(1260.47, 3714.75) * mm, "end": v(1108.07, 3714.75) * mm});
            skLineSegment(sketch, "E7.12.7.2", {"start": v(1108.07, 3559.17) * mm, "end": v(1717.67, 3559.17) * mm});
            skLineSegment(sketch, "E7.15.7.2", {"start": v(1104.9, 3559.17) * mm, "end": v(1104.9, 4168.77) * mm});
            skLineSegment(sketch, "E7.18.7.2", {"start": v(1108.07, 3711.57) * mm, "end": v(1717.67, 3711.57) * mm});
            skLineSegment(sketch, "E7.21.7.2", {"start": v(1260.47, 4324.35) * mm, "end": v(1108.07, 4324.35) * mm});
            skLineSegment(sketch, "E7.24.7.2", {"start": v(952.5, 3559.17) * mm, "end": v(952.5, 4168.77) * mm});
            skLineSegment(sketch, "E7.27.7.2", {"start": v(1108.07, 3714.75) * mm, "end": v(1108.07, 4324.35) * mm});
            skLineSegment(sketch, "E7.30.7.2", {"start": v(1562.1, 3403.6) * mm, "end": v(1562.1, 3556) * mm});
            skLineSegment(sketch, "E7.33.7.2", {"start": v(1260.47, 3714.75) * mm, "end": v(1260.47, 4324.35) * mm});
            skLineSegment(sketch, "E7.36.7.2", {"start": v(952.5, 3403.6) * mm, "end": v(952.5, 3556) * mm});
            skLineSegment(sketch, "E7.39.7.2", {"start": v(1104.9, 4168.77) * mm, "end": v(952.5, 4168.77) * mm});
            skLineSegment(sketch, "E7.42.7.2", {"start": v(1717.67, 3559.17) * mm, "end": v(1717.67, 3711.57) * mm});
            skLineSegment(sketch, "E7.45.7.2", {"start": v(952.5, 3556) * mm, "end": v(1562.1, 3556) * mm});
            skLineSegment(sketch, "E7.0.7.3", {"start": v(339.72, 4016.38) * mm, "end": v(949.32, 4016.38) * mm});
            skLineSegment(sketch, "E7.3.7.3", {"start": v(492.12, 4171.95) * mm, "end": v(339.72, 4171.95) * mm});
            skLineSegment(sketch, "E7.6.7.3", {"start": v(495.3, 4171.95) * mm, "end": v(495.3, 4324.35) * mm});
            skLineSegment(sketch, "E7.9.7.3", {"start": v(647.7, 4327.52) * mm, "end": v(495.3, 4327.52) * mm});
            skLineSegment(sketch, "E7.12.7.3", {"start": v(495.3, 4171.95) * mm, "end": v(1104.9, 4171.95) * mm});
            skLineSegment(sketch, "E7.15.7.3", {"start": v(492.12, 4171.95) * mm, "end": v(492.12, 4781.55) * mm});
            skLineSegment(sketch, "E7.18.7.3", {"start": v(495.3, 4324.35) * mm, "end": v(1104.9, 4324.35) * mm});
            skLineSegment(sketch, "E7.21.7.3", {"start": v(647.7, 4937.12) * mm, "end": v(495.3, 4937.12) * mm});
            skLineSegment(sketch, "E7.24.7.3", {"start": v(339.72, 4171.95) * mm, "end": v(339.72, 4781.55) * mm});
            skLineSegment(sketch, "E7.27.7.3", {"start": v(495.3, 4327.52) * mm, "end": v(495.3, 4937.12) * mm});
            skLineSegment(sketch, "E7.30.7.3", {"start": v(949.32, 4016.38) * mm, "end": v(949.32, 4168.78) * mm});
            skLineSegment(sketch, "E7.33.7.3", {"start": v(647.7, 4327.52) * mm, "end": v(647.7, 4937.12) * mm});
            skLineSegment(sketch, "E7.36.7.3", {"start": v(339.72, 4016.38) * mm, "end": v(339.72, 4168.78) * mm});
            skLineSegment(sketch, "E7.39.7.3", {"start": v(492.12, 4781.55) * mm, "end": v(339.72, 4781.55) * mm});
            skLineSegment(sketch, "E7.42.7.3", {"start": v(1104.9, 4171.95) * mm, "end": v(1104.9, 4324.35) * mm});
            skLineSegment(sketch, "E7.45.7.3", {"start": v(339.72, 4168.78) * mm, "end": v(949.32, 4168.78) * mm});
            skLineSegment(sketch, "E7.0.7.4", {"start": v(-273.05, 4629.15) * mm, "end": v(336.55, 4629.15) * mm});
            skLineSegment(sketch, "E7.3.7.4", {"start": v(-120.65, 4784.72) * mm, "end": v(-273.05, 4784.72) * mm});
            skLineSegment(sketch, "E7.6.7.4", {"start": v(-117.48, 4784.72) * mm, "end": v(-117.48, 4937.12) * mm});
            skLineSegment(sketch, "E7.9.7.4", {"start": v(34.92, 4940.3) * mm, "end": v(-117.48, 4940.3) * mm});
            skLineSegment(sketch, "E7.12.7.4", {"start": v(-117.48, 4784.72) * mm, "end": v(492.12, 4784.72) * mm});
            skLineSegment(sketch, "E7.15.7.4", {"start": v(-120.65, 4784.72) * mm, "end": v(-120.65, 5394.32) * mm});
            skLineSegment(sketch, "E7.18.7.4", {"start": v(-117.48, 4937.12) * mm, "end": v(492.12, 4937.12) * mm});
            skLineSegment(sketch, "E7.21.7.4", {"start": v(34.92, 5549.9) * mm, "end": v(-117.48, 5549.9) * mm});
            skLineSegment(sketch, "E7.24.7.4", {"start": v(-273.05, 4784.72) * mm, "end": v(-273.05, 5394.32) * mm});
            skLineSegment(sketch, "E7.27.7.4", {"start": v(-117.48, 4940.3) * mm, "end": v(-117.48, 5549.9) * mm});
            skLineSegment(sketch, "E7.30.7.4", {"start": v(336.55, 4629.15) * mm, "end": v(336.55, 4781.55) * mm});
            skLineSegment(sketch, "E7.33.7.4", {"start": v(34.92, 4940.3) * mm, "end": v(34.92, 5549.9) * mm});
            skLineSegment(sketch, "E7.36.7.4", {"start": v(-273.05, 4629.15) * mm, "end": v(-273.05, 4781.55) * mm});
            skLineSegment(sketch, "E7.39.7.4", {"start": v(-120.65, 5394.32) * mm, "end": v(-273.05, 5394.32) * mm});
            skLineSegment(sketch, "E7.42.7.4", {"start": v(492.12, 4784.72) * mm, "end": v(492.12, 4937.12) * mm});
            skLineSegment(sketch, "E7.45.7.4", {"start": v(-273.05, 4781.55) * mm, "end": v(336.55, 4781.55) * mm});
            skLineSegment(sketch, "E8.0.8.0", {"start": v(2489.2, 2489.2) * mm, "end": v(3098.8, 2489.2) * mm});
            skLineSegment(sketch, "E8.3.8.0", {"start": v(2641.6, 2644.77) * mm, "end": v(2489.2, 2644.77) * mm});
            skLineSegment(sketch, "E8.6.8.0", {"start": v(2644.78, 2644.77) * mm, "end": v(2644.78, 2797.17) * mm});
            skLineSegment(sketch, "E8.9.8.0", {"start": v(2797.18, 2800.35) * mm, "end": v(2644.78, 2800.35) * mm});
            skLineSegment(sketch, "E8.12.8.0", {"start": v(2644.78, 2644.77) * mm, "end": v(3254.38, 2644.77) * mm});
            skLineSegment(sketch, "E8.15.8.0", {"start": v(2641.6, 2644.77) * mm, "end": v(2641.6, 3254.37) * mm});
            skLineSegment(sketch, "E8.18.8.0", {"start": v(2644.78, 2797.17) * mm, "end": v(3254.38, 2797.17) * mm});
            skLineSegment(sketch, "E8.21.8.0", {"start": v(2797.18, 3409.95) * mm, "end": v(2644.78, 3409.95) * mm});
            skLineSegment(sketch, "E8.24.8.0", {"start": v(2489.2, 2644.77) * mm, "end": v(2489.2, 3254.37) * mm});
            skLineSegment(sketch, "E8.27.8.0", {"start": v(2644.78, 2800.35) * mm, "end": v(2644.78, 3409.95) * mm});
            skLineSegment(sketch, "E8.30.8.0", {"start": v(3098.8, 2489.2) * mm, "end": v(3098.8, 2641.6) * mm});
            skLineSegment(sketch, "E8.33.8.0", {"start": v(2797.18, 2800.35) * mm, "end": v(2797.18, 3409.95) * mm});
            skLineSegment(sketch, "E8.36.8.0", {"start": v(2489.2, 2489.2) * mm, "end": v(2489.2, 2641.6) * mm});
            skLineSegment(sketch, "E8.39.8.0", {"start": v(2641.6, 3254.37) * mm, "end": v(2489.2, 3254.37) * mm});
            skLineSegment(sketch, "E8.42.8.0", {"start": v(3254.38, 2644.77) * mm, "end": v(3254.38, 2797.17) * mm});
            skLineSegment(sketch, "E8.45.8.0", {"start": v(2489.2, 2641.6) * mm, "end": v(3098.8, 2641.6) * mm});
            skLineSegment(sketch, "E8.0.8.1", {"start": v(1876.43, 3101.97) * mm, "end": v(2486.03, 3101.97) * mm});
            skLineSegment(sketch, "E8.3.8.1", {"start": v(2028.83, 3257.55) * mm, "end": v(1876.43, 3257.55) * mm});
            skLineSegment(sketch, "E8.6.8.1", {"start": v(2032, 3257.55) * mm, "end": v(2032, 3409.95) * mm});
            skLineSegment(sketch, "E8.9.8.1", {"start": v(2184.4, 3413.12) * mm, "end": v(2032, 3413.12) * mm});
            skLineSegment(sketch, "E8.12.8.1", {"start": v(2032, 3257.55) * mm, "end": v(2641.6, 3257.55) * mm});
            skLineSegment(sketch, "E8.15.8.1", {"start": v(2028.83, 3257.55) * mm, "end": v(2028.83, 3867.15) * mm});
            skLineSegment(sketch, "E8.18.8.1", {"start": v(2032, 3409.95) * mm, "end": v(2641.6, 3409.95) * mm});
            skLineSegment(sketch, "E8.21.8.1", {"start": v(2184.4, 4022.72) * mm, "end": v(2032, 4022.72) * mm});
            skLineSegment(sketch, "E8.24.8.1", {"start": v(1876.43, 3257.55) * mm, "end": v(1876.43, 3867.15) * mm});
            skLineSegment(sketch, "E8.27.8.1", {"start": v(2032, 3413.12) * mm, "end": v(2032, 4022.72) * mm});
            skLineSegment(sketch, "E8.30.8.1", {"start": v(2486.03, 3101.97) * mm, "end": v(2486.03, 3254.37) * mm});
            skLineSegment(sketch, "E8.33.8.1", {"start": v(2184.4, 3413.12) * mm, "end": v(2184.4, 4022.72) * mm});
            skLineSegment(sketch, "E8.36.8.1", {"start": v(1876.43, 3101.97) * mm, "end": v(1876.43, 3254.37) * mm});
            skLineSegment(sketch, "E8.39.8.1", {"start": v(2028.83, 3867.15) * mm, "end": v(1876.43, 3867.15) * mm});
            skLineSegment(sketch, "E8.42.8.1", {"start": v(2641.6, 3257.55) * mm, "end": v(2641.6, 3409.95) * mm});
            skLineSegment(sketch, "E8.45.8.1", {"start": v(1876.43, 3254.37) * mm, "end": v(2486.03, 3254.37) * mm});
            skLineSegment(sketch, "E8.0.8.2", {"start": v(1263.65, 3714.75) * mm, "end": v(1873.25, 3714.75) * mm});
            skLineSegment(sketch, "E8.3.8.2", {"start": v(1416.05, 3870.32) * mm, "end": v(1263.65, 3870.32) * mm});
            skLineSegment(sketch, "E8.6.8.2", {"start": v(1419.22, 3870.32) * mm, "end": v(1419.22, 4022.72) * mm});
            skLineSegment(sketch, "E8.9.8.2", {"start": v(1571.62, 4025.9) * mm, "end": v(1419.22, 4025.9) * mm});
            skLineSegment(sketch, "E8.12.8.2", {"start": v(1419.22, 3870.32) * mm, "end": v(2028.82, 3870.32) * mm});
            skLineSegment(sketch, "E8.15.8.2", {"start": v(1416.05, 3870.32) * mm, "end": v(1416.05, 4479.92) * mm});
            skLineSegment(sketch, "E8.18.8.2", {"start": v(1419.22, 4022.72) * mm, "end": v(2028.82, 4022.72) * mm});
            skLineSegment(sketch, "E8.21.8.2", {"start": v(1571.62, 4635.5) * mm, "end": v(1419.22, 4635.5) * mm});
            skLineSegment(sketch, "E8.24.8.2", {"start": v(1263.65, 3870.32) * mm, "end": v(1263.65, 4479.92) * mm});
            skLineSegment(sketch, "E8.27.8.2", {"start": v(1419.22, 4025.9) * mm, "end": v(1419.22, 4635.5) * mm});
            skLineSegment(sketch, "E8.30.8.2", {"start": v(1873.25, 3714.75) * mm, "end": v(1873.25, 3867.15) * mm});
            skLineSegment(sketch, "E8.33.8.2", {"start": v(1571.62, 4025.9) * mm, "end": v(1571.62, 4635.5) * mm});
            skLineSegment(sketch, "E8.36.8.2", {"start": v(1263.65, 3714.75) * mm, "end": v(1263.65, 3867.15) * mm});
            skLineSegment(sketch, "E8.39.8.2", {"start": v(1416.05, 4479.92) * mm, "end": v(1263.65, 4479.92) * mm});
            skLineSegment(sketch, "E8.42.8.2", {"start": v(2028.82, 3870.32) * mm, "end": v(2028.82, 4022.72) * mm});
            skLineSegment(sketch, "E8.45.8.2", {"start": v(1263.65, 3867.15) * mm, "end": v(1873.25, 3867.15) * mm});
            skLineSegment(sketch, "E8.0.8.3", {"start": v(650.87, 4327.52) * mm, "end": v(1260.47, 4327.52) * mm});
            skLineSegment(sketch, "E8.3.8.3", {"start": v(803.27, 4483.1) * mm, "end": v(650.87, 4483.1) * mm});
            skLineSegment(sketch, "E8.6.8.3", {"start": v(806.45, 4483.1) * mm, "end": v(806.45, 4635.5) * mm});
            skLineSegment(sketch, "E8.9.8.3", {"start": v(958.85, 4638.67) * mm, "end": v(806.45, 4638.67) * mm});
            skLineSegment(sketch, "E8.12.8.3", {"start": v(806.45, 4483.1) * mm, "end": v(1416.05, 4483.1) * mm});
            skLineSegment(sketch, "E8.15.8.3", {"start": v(803.27, 4483.1) * mm, "end": v(803.27, 5092.7) * mm});
            skLineSegment(sketch, "E8.18.8.3", {"start": v(806.45, 4635.5) * mm, "end": v(1416.05, 4635.5) * mm});
            skLineSegment(sketch, "E8.21.8.3", {"start": v(958.85, 5248.27) * mm, "end": v(806.45, 5248.27) * mm});
            skLineSegment(sketch, "E8.24.8.3", {"start": v(650.87, 4483.1) * mm, "end": v(650.87, 5092.7) * mm});
            skLineSegment(sketch, "E8.27.8.3", {"start": v(806.45, 4638.67) * mm, "end": v(806.45, 5248.27) * mm});
            skLineSegment(sketch, "E8.30.8.3", {"start": v(1260.47, 4327.52) * mm, "end": v(1260.47, 4479.92) * mm});
            skLineSegment(sketch, "E8.33.8.3", {"start": v(958.85, 4638.67) * mm, "end": v(958.85, 5248.27) * mm});
            skLineSegment(sketch, "E8.36.8.3", {"start": v(650.87, 4327.52) * mm, "end": v(650.87, 4479.92) * mm});
            skLineSegment(sketch, "E8.39.8.3", {"start": v(803.27, 5092.7) * mm, "end": v(650.87, 5092.7) * mm});
            skLineSegment(sketch, "E8.42.8.3", {"start": v(1416.05, 4483.1) * mm, "end": v(1416.05, 4635.5) * mm});
            skLineSegment(sketch, "E8.45.8.3", {"start": v(650.87, 4479.92) * mm, "end": v(1260.47, 4479.92) * mm});
            skLineSegment(sketch, "E8.0.8.4", {"start": v(38.1, 4940.3) * mm, "end": v(647.7, 4940.3) * mm});
            skLineSegment(sketch, "E8.3.8.4", {"start": v(190.5, 5095.87) * mm, "end": v(38.1, 5095.87) * mm});
            skLineSegment(sketch, "E8.6.8.4", {"start": v(193.67, 5095.87) * mm, "end": v(193.67, 5248.27) * mm});
            skLineSegment(sketch, "E8.9.8.4", {"start": v(346.07, 5251.45) * mm, "end": v(193.67, 5251.45) * mm});
            skLineSegment(sketch, "E8.12.8.4", {"start": v(193.67, 5095.87) * mm, "end": v(803.27, 5095.87) * mm});
            skLineSegment(sketch, "E8.15.8.4", {"start": v(190.5, 5095.87) * mm, "end": v(190.5, 5705.47) * mm});
            skLineSegment(sketch, "E8.18.8.4", {"start": v(193.67, 5248.27) * mm, "end": v(803.27, 5248.27) * mm});
            skLineSegment(sketch, "E8.21.8.4", {"start": v(346.07, 5861.05) * mm, "end": v(193.67, 5861.05) * mm});
            skLineSegment(sketch, "E8.24.8.4", {"start": v(38.1, 5095.87) * mm, "end": v(38.1, 5705.47) * mm});
            skLineSegment(sketch, "E8.27.8.4", {"start": v(193.67, 5251.45) * mm, "end": v(193.67, 5861.05) * mm});
            skLineSegment(sketch, "E8.30.8.4", {"start": v(647.7, 4940.3) * mm, "end": v(647.7, 5092.7) * mm});
            skLineSegment(sketch, "E8.33.8.4", {"start": v(346.07, 5251.45) * mm, "end": v(346.07, 5861.05) * mm});
            skLineSegment(sketch, "E8.36.8.4", {"start": v(38.1, 4940.3) * mm, "end": v(38.1, 5092.7) * mm});
            skLineSegment(sketch, "E8.39.8.4", {"start": v(190.5, 5705.47) * mm, "end": v(38.1, 5705.47) * mm});
            skLineSegment(sketch, "E8.42.8.4", {"start": v(803.27, 5095.87) * mm, "end": v(803.27, 5248.27) * mm});
            skLineSegment(sketch, "E8.45.8.4", {"start": v(38.1, 5092.7) * mm, "end": v(647.7, 5092.7) * mm});
            skSolve(sketch);
        }
        {
            var Q0;
            Q0=qSketchRegion(id+"F0",true);
            extrude(context, id + "F1", {"entities" : qUnion([Q0]), "depth" : 6.35 * mm, "offsetDistance" : 25.4 * mm});
        }
        {
            var Q0;
            Q0=qCreatedBy(makeId("Top.planeOp"),FACE);
            var sketch = newSketch(context, id + "F2", { "sketchPlane" : qUnion([Q0])});
            skLineSegment(sketch, "E9", {"start": v(-267.36, 4162.97) * mm, "end": v(-1367.44, 3062.89) * mm});
            skLineSegment(sketch, "E10", {"start": v(-1367.44, 3062.89) * mm, "end": v(-78.77, 1774.22) * mm});
            skLineSegment(sketch, "E11", {"start": v(-78.77, 1774.22) * mm, "end": v(1021.3, 2874.3) * mm});
            skLineSegment(sketch, "E12", {"start": v(1021.3, 2874.3) * mm, "end": v(-267.36, 4162.97) * mm});
            skLineSegment(sketch, "E13.bottom", {"start": v(-4816.06, 8587.4) * mm, "end": v(6787.9, 8587.4) * mm});
            skLineSegment(sketch, "E13.top", {"start": v(-4816.06, -1489.72) * mm, "end": v(6787.9, -1489.72) * mm});
            skLineSegment(sketch, "E13.left", {"start": v(-4816.06, 8587.4) * mm, "end": v(-4816.06, -1489.72) * mm});
            skLineSegment(sketch, "E13.right", {"start": v(6787.9, 8587.4) * mm, "end": v(6787.9, -1489.72) * mm});
            skLineSegment(sketch, "E14", {"start": v(327.03, 3546.47) * mm, "end": v(171.45, 3390.9) * mm, "construction": true});
            skLineSegment(sketch, "E15", {"start": v(327.03, 3390.9) * mm, "end": v(171.45, 3235.32) * mm, "construction": true});
            skLineSegment(sketch, "E16", {"start": v(205.93, 3425.38) * mm, "end": v(283.71, 3347.59) * mm, "construction": true});
            skLineSegment(sketch, "E17", {"start": v(376.98, 3518.64) * mm, "end": v(244.82, 3386.48) * mm, "construction": true});
            skSolve(sketch);
        }
        {
            var Q0;
            Q0=qSketchRegion(id+"F2",true);
            extrude(context, id + "F3", {"entities" : qUnion([Q0]), "operationType" : NewBodyOperationType.REMOVE, "endBound" : BoundingType.THROUGH_ALL, "depth" : 25.4 * mm, "offsetDistance" : 25.4 * mm});
        }
        {
            var Q0;
            Q0=makeQuery(id+"F1.opExtrude","SWEPT_BODY",BODY,{"disambiguationData":[OSD([sQuery(id+"F0.wireOp",EDGE,"E4.1.1.3"),sQuery(id+"F0.wireOp",EDGE,"E4.1.1.7"),sQuery(id+"F0.wireOp",EDGE,"E4.1.1.9"),sQuery(id+"F0.wireOp",EDGE,"E4.1.1.11")])]});
            var Q1;
            Q1=makeQuery(id+"F1.opExtrude","SWEPT_BODY",BODY,{"disambiguationData":[OSD([sQuery(id+"F0.wireOp",EDGE,"E4.2.1.1"),sQuery(id+"F0.wireOp",EDGE,"E4.2.1.5"),sQuery(id+"F0.wireOp",EDGE,"E4.2.1.8"),sQuery(id+"F0.wireOp",EDGE,"E4.2.1.13")])]});
            var Q2;
            Q2=makeQuery(id+"F1.opExtrude","SWEPT_BODY",BODY,{"disambiguationData":[OSD([sQuery(id+"F0.wireOp",EDGE,"E4.2.1.3"),sQuery(id+"F0.wireOp",EDGE,"E4.2.1.7"),sQuery(id+"F0.wireOp",EDGE,"E4.2.1.9"),sQuery(id+"F0.wireOp",EDGE,"E4.2.1.11")])]});
            var Q3;
            Q3=makeQuery(id+"F1.opExtrude","SWEPT_BODY",BODY,{"disambiguationData":[OSD([sQuery(id+"F0.wireOp",EDGE,"E5.3.3.1"),sQuery(id+"F0.wireOp",EDGE,"E5.15.3.1"),sQuery(id+"F0.wireOp",EDGE,"E5.24.3.1"),sQuery(id+"F0.wireOp",EDGE,"E5.39.3.1")])]});
            var Q4;
            Q4=makeQuery(id+"F1.opExtrude","SWEPT_BODY",BODY,{"disambiguationData":[OSD([sQuery(id+"F0.wireOp",EDGE,"E5.9.3.1"),sQuery(id+"F0.wireOp",EDGE,"E5.21.3.1"),sQuery(id+"F0.wireOp",EDGE,"E5.27.3.1"),sQuery(id+"F0.wireOp",EDGE,"E5.33.3.1")])]});
            var Q5;
            Q5=makeQuery(id+"F1.opExtrude","SWEPT_BODY",BODY,{"disambiguationData":[OSD([sQuery(id+"F0.wireOp",EDGE,"E5.3.4.1"),sQuery(id+"F0.wireOp",EDGE,"E5.15.4.1"),sQuery(id+"F0.wireOp",EDGE,"E5.24.4.1"),sQuery(id+"F0.wireOp",EDGE,"E5.39.4.1")])]});
            var Q6;
            Q6=makeQuery(id+"F1.opExtrude","SWEPT_BODY",BODY,{"disambiguationData":[OSD([sQuery(id+"F0.wireOp",EDGE,"E5.9.4.1"),sQuery(id+"F0.wireOp",EDGE,"E5.21.4.1"),sQuery(id+"F0.wireOp",EDGE,"E5.27.4.1"),sQuery(id+"F0.wireOp",EDGE,"E5.33.4.1")])]});
            var Q7;
            Q7=makeQuery(id+"F1.opExtrude","SWEPT_BODY",BODY,{"disambiguationData":[OSD([sQuery(id+"F0.wireOp",EDGE,"E5.3.5.1"),sQuery(id+"F0.wireOp",EDGE,"E5.15.5.1"),sQuery(id+"F0.wireOp",EDGE,"E5.24.5.1"),sQuery(id+"F0.wireOp",EDGE,"E5.39.5.1")])]});
            var Q8;
            Q8=makeQuery(id+"F1.opExtrude","SWEPT_BODY",BODY,{"disambiguationData":[OSD([sQuery(id+"F0.wireOp",EDGE,"E6.9.1.2"),sQuery(id+"F0.wireOp",EDGE,"E6.21.1.2"),sQuery(id+"F0.wireOp",EDGE,"E6.27.1.2"),sQuery(id+"F0.wireOp",EDGE,"E6.33.1.2")])]});
            var Q9;
            Q9=makeQuery(id+"F1.opExtrude","SWEPT_BODY",BODY,{"disambiguationData":[OSD([sQuery(id+"F0.wireOp",EDGE,"E6.9.1.3"),sQuery(id+"F0.wireOp",EDGE,"E6.21.1.3"),sQuery(id+"F0.wireOp",EDGE,"E6.27.1.3"),sQuery(id+"F0.wireOp",EDGE,"E6.33.1.3")])]});
            var Q10;
            Q10=makeQuery(id+"F1.opExtrude","SWEPT_BODY",BODY,{"disambiguationData":[OSD([sQuery(id+"F0.wireOp",EDGE,"E6.0.2.2"),sQuery(id+"F0.wireOp",EDGE,"E6.30.2.2"),sQuery(id+"F0.wireOp",EDGE,"E6.36.2.2"),sQuery(id+"F0.wireOp",EDGE,"E6.45.2.2")])]});
            var Q11;
            Q11=makeQuery(id+"F1.opExtrude","SWEPT_BODY",BODY,{"disambiguationData":[OSD([sQuery(id+"F0.wireOp",EDGE,"E6.3.2.2"),sQuery(id+"F0.wireOp",EDGE,"E6.15.2.2"),sQuery(id+"F0.wireOp",EDGE,"E6.24.2.2"),sQuery(id+"F0.wireOp",EDGE,"E6.39.2.2")])]});
            var Q12;
            Q12=makeQuery(id+"F1.opExtrude","SWEPT_BODY",BODY,{"disambiguationData":[OSD([sQuery(id+"F0.wireOp",EDGE,"E6.6.2.2"),sQuery(id+"F0.wireOp",EDGE,"E6.12.2.2"),sQuery(id+"F0.wireOp",EDGE,"E6.18.2.2"),sQuery(id+"F0.wireOp",EDGE,"E6.42.2.2")])]});
            var Q13;
            Q13=makeQuery(id+"F1.opExtrude","SWEPT_BODY",BODY,{"disambiguationData":[OSD([sQuery(id+"F0.wireOp",EDGE,"E6.9.2.2"),sQuery(id+"F0.wireOp",EDGE,"E6.21.2.2"),sQuery(id+"F0.wireOp",EDGE,"E6.27.2.2"),sQuery(id+"F0.wireOp",EDGE,"E6.33.2.2")])]});
            var Q14;
            Q14=makeQuery(id+"F1.opExtrude","SWEPT_BODY",BODY,{"disambiguationData":[OSD([sQuery(id+"F0.wireOp",EDGE,"E6.0.2.3"),sQuery(id+"F0.wireOp",EDGE,"E6.30.2.3"),sQuery(id+"F0.wireOp",EDGE,"E6.36.2.3"),sQuery(id+"F0.wireOp",EDGE,"E6.45.2.3")])]});
            var Q15;
            Q15=makeQuery(id+"F1.opExtrude","SWEPT_BODY",BODY,{"disambiguationData":[OSD([sQuery(id+"F0.wireOp",EDGE,"E6.3.2.3"),sQuery(id+"F0.wireOp",EDGE,"E6.15.2.3"),sQuery(id+"F0.wireOp",EDGE,"E6.24.2.3"),sQuery(id+"F0.wireOp",EDGE,"E6.39.2.3")])]});
            var Q16;
            Q16=makeQuery(id+"F1.opExtrude","SWEPT_BODY",BODY,{"disambiguationData":[OSD([sQuery(id+"F0.wireOp",EDGE,"E6.6.2.3"),sQuery(id+"F0.wireOp",EDGE,"E6.12.2.3"),sQuery(id+"F0.wireOp",EDGE,"E6.18.2.3"),sQuery(id+"F0.wireOp",EDGE,"E6.42.2.3")])]});
            var Q17;
            Q17=makeQuery(id+"F1.opExtrude","SWEPT_BODY",BODY,{"disambiguationData":[OSD([sQuery(id+"F0.wireOp",EDGE,"E6.9.2.3"),sQuery(id+"F0.wireOp",EDGE,"E6.21.2.3"),sQuery(id+"F0.wireOp",EDGE,"E6.27.2.3"),sQuery(id+"F0.wireOp",EDGE,"E6.33.2.3")])]});
            var Q18;
            Q18=makeQuery(id+"F1.opExtrude","SWEPT_BODY",BODY,{"disambiguationData":[OSD([sQuery(id+"F0.wireOp",EDGE,"E6.0.2.4"),sQuery(id+"F0.wireOp",EDGE,"E6.30.2.4"),sQuery(id+"F0.wireOp",EDGE,"E6.36.2.4"),sQuery(id+"F0.wireOp",EDGE,"E6.45.2.4")])]});
            var Q19;
            Q19=makeQuery(id+"F1.opExtrude","SWEPT_BODY",BODY,{"disambiguationData":[OSD([sQuery(id+"F0.wireOp",EDGE,"E6.6.2.4"),sQuery(id+"F0.wireOp",EDGE,"E6.12.2.4"),sQuery(id+"F0.wireOp",EDGE,"E6.18.2.4"),sQuery(id+"F0.wireOp",EDGE,"E6.42.2.4")])]});
            var Q20;
            Q20=makeQuery(id+"F1.opExtrude","SWEPT_BODY",BODY,{"disambiguationData":[OSD([sQuery(id+"F0.wireOp",EDGE,"E6.0.3.2"),sQuery(id+"F0.wireOp",EDGE,"E6.30.3.2"),sQuery(id+"F0.wireOp",EDGE,"E6.36.3.2"),sQuery(id+"F0.wireOp",EDGE,"E6.45.3.2")])]});
            var Q21;
            Q21=makeQuery(id+"F1.opExtrude","SWEPT_BODY",BODY,{"disambiguationData":[OSD([sQuery(id+"F0.wireOp",EDGE,"E6.3.3.2"),sQuery(id+"F0.wireOp",EDGE,"E6.15.3.2"),sQuery(id+"F0.wireOp",EDGE,"E6.24.3.2"),sQuery(id+"F0.wireOp",EDGE,"E6.39.3.2")])]});
            var Q22;
            Q22=makeQuery(id+"F1.opExtrude","SWEPT_BODY",BODY,{"disambiguationData":[OSD([sQuery(id+"F0.wireOp",EDGE,"E6.6.3.2"),sQuery(id+"F0.wireOp",EDGE,"E6.12.3.2"),sQuery(id+"F0.wireOp",EDGE,"E6.18.3.2"),sQuery(id+"F0.wireOp",EDGE,"E6.42.3.2")])]});
            var Q23;
            Q23=makeQuery(id+"F1.opExtrude","SWEPT_BODY",BODY,{"disambiguationData":[OSD([sQuery(id+"F0.wireOp",EDGE,"E6.9.3.2"),sQuery(id+"F0.wireOp",EDGE,"E6.21.3.2"),sQuery(id+"F0.wireOp",EDGE,"E6.27.3.2"),sQuery(id+"F0.wireOp",EDGE,"E6.33.3.2")])]});
            var Q24;
            Q24=makeQuery(id+"F1.opExtrude","SWEPT_BODY",BODY,{"disambiguationData":[OSD([sQuery(id+"F0.wireOp",EDGE,"E6.0.3.3"),sQuery(id+"F0.wireOp",EDGE,"E6.30.3.3"),sQuery(id+"F0.wireOp",EDGE,"E6.36.3.3"),sQuery(id+"F0.wireOp",EDGE,"E6.45.3.3")])]});
            var Q25;
            Q25=makeQuery(id+"F1.opExtrude","SWEPT_BODY",BODY,{"disambiguationData":[OSD([sQuery(id+"F0.wireOp",EDGE,"E6.3.3.3"),sQuery(id+"F0.wireOp",EDGE,"E6.15.3.3"),sQuery(id+"F0.wireOp",EDGE,"E6.24.3.3"),sQuery(id+"F0.wireOp",EDGE,"E6.39.3.3")])]});
            var Q26;
            Q26=makeQuery(id+"F1.opExtrude","SWEPT_BODY",BODY,{"disambiguationData":[OSD([sQuery(id+"F0.wireOp",EDGE,"E6.6.3.3"),sQuery(id+"F0.wireOp",EDGE,"E6.12.3.3"),sQuery(id+"F0.wireOp",EDGE,"E6.18.3.3"),sQuery(id+"F0.wireOp",EDGE,"E6.42.3.3")])]});
            var Q27;
            Q27=makeQuery(id+"F1.opExtrude","SWEPT_BODY",BODY,{"disambiguationData":[OSD([sQuery(id+"F0.wireOp",EDGE,"E6.9.3.3"),sQuery(id+"F0.wireOp",EDGE,"E6.21.3.3"),sQuery(id+"F0.wireOp",EDGE,"E6.27.3.3"),sQuery(id+"F0.wireOp",EDGE,"E6.33.3.3")])]});
            var Q28;
            Q28=makeQuery(id+"F1.opExtrude","SWEPT_BODY",BODY,{"disambiguationData":[OSD([sQuery(id+"F0.wireOp",EDGE,"E6.0.3.4"),sQuery(id+"F0.wireOp",EDGE,"E6.30.3.4"),sQuery(id+"F0.wireOp",EDGE,"E6.36.3.4"),sQuery(id+"F0.wireOp",EDGE,"E6.45.3.4")])]});
            var Q29;
            Q29=makeQuery(id+"F1.opExtrude","SWEPT_BODY",BODY,{"disambiguationData":[OSD([sQuery(id+"F0.wireOp",EDGE,"E6.6.3.4"),sQuery(id+"F0.wireOp",EDGE,"E6.12.3.4"),sQuery(id+"F0.wireOp",EDGE,"E6.18.3.4"),sQuery(id+"F0.wireOp",EDGE,"E6.42.3.4")])]});
            var Q30;
            Q30=makeQuery(id+"F1.opExtrude","SWEPT_BODY",BODY,{"disambiguationData":[OSD([sQuery(id+"F0.wireOp",EDGE,"E6.0.4.2"),sQuery(id+"F0.wireOp",EDGE,"E6.30.4.2"),sQuery(id+"F0.wireOp",EDGE,"E6.36.4.2"),sQuery(id+"F0.wireOp",EDGE,"E6.45.4.2")])]});
            var Q31;
            Q31=makeQuery(id+"F1.opExtrude","SWEPT_BODY",BODY,{"disambiguationData":[OSD([sQuery(id+"F0.wireOp",EDGE,"E6.3.4.2"),sQuery(id+"F0.wireOp",EDGE,"E6.15.4.2"),sQuery(id+"F0.wireOp",EDGE,"E6.24.4.2"),sQuery(id+"F0.wireOp",EDGE,"E6.39.4.2")])]});
            var Q32;
            Q32=makeQuery(id+"F1.opExtrude","SWEPT_BODY",BODY,{"disambiguationData":[OSD([sQuery(id+"F0.wireOp",EDGE,"E6.6.4.2"),sQuery(id+"F0.wireOp",EDGE,"E6.12.4.2"),sQuery(id+"F0.wireOp",EDGE,"E6.18.4.2"),sQuery(id+"F0.wireOp",EDGE,"E6.42.4.2")])]});
            var Q33;
            Q33=makeQuery(id+"F1.opExtrude","SWEPT_BODY",BODY,{"disambiguationData":[OSD([sQuery(id+"F0.wireOp",EDGE,"E6.9.4.2"),sQuery(id+"F0.wireOp",EDGE,"E6.21.4.2"),sQuery(id+"F0.wireOp",EDGE,"E6.27.4.2"),sQuery(id+"F0.wireOp",EDGE,"E6.33.4.2")])]});
            var Q34;
            Q34=makeQuery(id+"F1.opExtrude","SWEPT_BODY",BODY,{"disambiguationData":[OSD([sQuery(id+"F0.wireOp",EDGE,"E6.0.4.3"),sQuery(id+"F0.wireOp",EDGE,"E6.30.4.3"),sQuery(id+"F0.wireOp",EDGE,"E6.36.4.3"),sQuery(id+"F0.wireOp",EDGE,"E6.45.4.3")])]});
            var Q35;
            Q35=makeQuery(id+"F1.opExtrude","SWEPT_BODY",BODY,{"disambiguationData":[OSD([sQuery(id+"F0.wireOp",EDGE,"E6.3.4.3"),sQuery(id+"F0.wireOp",EDGE,"E6.15.4.3"),sQuery(id+"F0.wireOp",EDGE,"E6.24.4.3"),sQuery(id+"F0.wireOp",EDGE,"E6.39.4.3")])]});
            var Q36;
            Q36=makeQuery(id+"F1.opExtrude","SWEPT_BODY",BODY,{"disambiguationData":[OSD([sQuery(id+"F0.wireOp",EDGE,"E6.6.4.3"),sQuery(id+"F0.wireOp",EDGE,"E6.12.4.3"),sQuery(id+"F0.wireOp",EDGE,"E6.18.4.3"),sQuery(id+"F0.wireOp",EDGE,"E6.42.4.3")])]});
            var Q37;
            Q37=makeQuery(id+"F1.opExtrude","SWEPT_BODY",BODY,{"disambiguationData":[OSD([sQuery(id+"F0.wireOp",EDGE,"E6.9.4.3"),sQuery(id+"F0.wireOp",EDGE,"E6.21.4.3"),sQuery(id+"F0.wireOp",EDGE,"E6.27.4.3"),sQuery(id+"F0.wireOp",EDGE,"E6.33.4.3")])]});
            var Q38;
            Q38=makeQuery(id+"F1.opExtrude","SWEPT_BODY",BODY,{"disambiguationData":[OSD([sQuery(id+"F0.wireOp",EDGE,"E6.0.4.4"),sQuery(id+"F0.wireOp",EDGE,"E6.30.4.4"),sQuery(id+"F0.wireOp",EDGE,"E6.36.4.4"),sQuery(id+"F0.wireOp",EDGE,"E6.45.4.4")])]});
            var Q39;
            Q39=makeQuery(id+"F1.opExtrude","SWEPT_BODY",BODY,{"disambiguationData":[OSD([sQuery(id+"F0.wireOp",EDGE,"E6.6.4.4"),sQuery(id+"F0.wireOp",EDGE,"E6.12.4.4"),sQuery(id+"F0.wireOp",EDGE,"E6.18.4.4"),sQuery(id+"F0.wireOp",EDGE,"E6.42.4.4")])]});
            var Q40;
            Q40=makeQuery(id+"F1.opExtrude","SWEPT_BODY",BODY,{"disambiguationData":[OSD([sQuery(id+"F0.wireOp",EDGE,"E6.0.5.2"),sQuery(id+"F0.wireOp",EDGE,"E6.30.5.2"),sQuery(id+"F0.wireOp",EDGE,"E6.36.5.2"),sQuery(id+"F0.wireOp",EDGE,"E6.45.5.2")])]});
            var Q41;
            Q41=makeQuery(id+"F1.opExtrude","SWEPT_BODY",BODY,{"disambiguationData":[OSD([sQuery(id+"F0.wireOp",EDGE,"E6.3.5.2"),sQuery(id+"F0.wireOp",EDGE,"E6.15.5.2"),sQuery(id+"F0.wireOp",EDGE,"E6.24.5.2"),sQuery(id+"F0.wireOp",EDGE,"E6.39.5.2")])]});
            var Q42;
            Q42=makeQuery(id+"F1.opExtrude","SWEPT_BODY",BODY,{"disambiguationData":[OSD([sQuery(id+"F0.wireOp",EDGE,"E6.6.5.2"),sQuery(id+"F0.wireOp",EDGE,"E6.12.5.2"),sQuery(id+"F0.wireOp",EDGE,"E6.18.5.2"),sQuery(id+"F0.wireOp",EDGE,"E6.42.5.2")])]});
            var Q43;
            Q43=makeQuery(id+"F1.opExtrude","SWEPT_BODY",BODY,{"disambiguationData":[OSD([sQuery(id+"F0.wireOp",EDGE,"E6.9.5.2"),sQuery(id+"F0.wireOp",EDGE,"E6.21.5.2"),sQuery(id+"F0.wireOp",EDGE,"E6.27.5.2"),sQuery(id+"F0.wireOp",EDGE,"E6.33.5.2")])]});
            var Q44;
            Q44=makeQuery(id+"F1.opExtrude","SWEPT_BODY",BODY,{"disambiguationData":[OSD([sQuery(id+"F0.wireOp",EDGE,"E6.0.5.3"),sQuery(id+"F0.wireOp",EDGE,"E6.30.5.3"),sQuery(id+"F0.wireOp",EDGE,"E6.36.5.3"),sQuery(id+"F0.wireOp",EDGE,"E6.45.5.3")])]});
            var Q45;
            Q45=makeQuery(id+"F1.opExtrude","SWEPT_BODY",BODY,{"disambiguationData":[OSD([sQuery(id+"F0.wireOp",EDGE,"E6.3.5.3"),sQuery(id+"F0.wireOp",EDGE,"E6.15.5.3"),sQuery(id+"F0.wireOp",EDGE,"E6.24.5.3"),sQuery(id+"F0.wireOp",EDGE,"E6.39.5.3")])]});
            var Q46;
            Q46=makeQuery(id+"F1.opExtrude","SWEPT_BODY",BODY,{"disambiguationData":[OSD([sQuery(id+"F0.wireOp",EDGE,"E6.6.5.3"),sQuery(id+"F0.wireOp",EDGE,"E6.12.5.3"),sQuery(id+"F0.wireOp",EDGE,"E6.18.5.3"),sQuery(id+"F0.wireOp",EDGE,"E6.42.5.3")])]});
            var Q47;
            Q47=makeQuery(id+"F1.opExtrude","SWEPT_BODY",BODY,{"disambiguationData":[OSD([sQuery(id+"F0.wireOp",EDGE,"E6.9.5.3"),sQuery(id+"F0.wireOp",EDGE,"E6.21.5.3"),sQuery(id+"F0.wireOp",EDGE,"E6.27.5.3"),sQuery(id+"F0.wireOp",EDGE,"E6.33.5.3")])]});
            var Q48;
            Q48=makeQuery(id+"F1.opExtrude","SWEPT_BODY",BODY,{"disambiguationData":[OSD([sQuery(id+"F0.wireOp",EDGE,"E6.0.5.4"),sQuery(id+"F0.wireOp",EDGE,"E6.30.5.4"),sQuery(id+"F0.wireOp",EDGE,"E6.36.5.4"),sQuery(id+"F0.wireOp",EDGE,"E6.45.5.4")])]});
            var Q49;
            Q49=makeQuery(id+"F1.opExtrude","SWEPT_BODY",BODY,{"disambiguationData":[OSD([sQuery(id+"F0.wireOp",EDGE,"E6.6.5.4"),sQuery(id+"F0.wireOp",EDGE,"E6.12.5.4"),sQuery(id+"F0.wireOp",EDGE,"E6.18.5.4"),sQuery(id+"F0.wireOp",EDGE,"E6.42.5.4")])]});
            var Q50;
            Q50=makeQuery(id+"F1.opExtrude","SWEPT_BODY",BODY,{"disambiguationData":[OSD([sQuery(id+"F0.wireOp",EDGE,"E7.0.6.2"),sQuery(id+"F0.wireOp",EDGE,"E7.30.6.2"),sQuery(id+"F0.wireOp",EDGE,"E7.36.6.2"),sQuery(id+"F0.wireOp",EDGE,"E7.45.6.2")])]});
            var Q51;
            Q51=makeQuery(id+"F1.opExtrude","SWEPT_BODY",BODY,{"disambiguationData":[OSD([sQuery(id+"F0.wireOp",EDGE,"E7.0.6.3"),sQuery(id+"F0.wireOp",EDGE,"E7.30.6.3"),sQuery(id+"F0.wireOp",EDGE,"E7.36.6.3"),sQuery(id+"F0.wireOp",EDGE,"E7.45.6.3")])]});
            var Q52;
            Q52=makeQuery(id+"F1.opExtrude","SWEPT_BODY",BODY,{"disambiguationData":[OSD([sQuery(id+"F0.wireOp",EDGE,"E7.3.6.2"),sQuery(id+"F0.wireOp",EDGE,"E7.15.6.2"),sQuery(id+"F0.wireOp",EDGE,"E7.24.6.2"),sQuery(id+"F0.wireOp",EDGE,"E7.39.6.2")])]});
            var Q53;
            Q53=makeQuery(id+"F1.opExtrude","SWEPT_BODY",BODY,{"disambiguationData":[OSD([sQuery(id+"F0.wireOp",EDGE,"E7.3.6.3"),sQuery(id+"F0.wireOp",EDGE,"E7.15.6.3"),sQuery(id+"F0.wireOp",EDGE,"E7.24.6.3"),sQuery(id+"F0.wireOp",EDGE,"E7.39.6.3")])]});
            var Q54;
            Q54=makeQuery(id+"F3.boolean.opBoolean","COPY",EDGE,{"derivedFrom":makeQuery(id+"F3.opExtrude","SWEPT_EDGE",EDGE,{"disambiguationData":[OSD([sQuery(id+"F2.wireOp",EDGE,"E9"),sQuery(id+"F2.wireOp",EDGE,"E10")])]})});
            transform(context, id + "F4", {"entities" : qUnion([Q0, Q1, Q2, Q3, Q4, Q5, Q6, Q7, Q8, Q9, Q10, Q11, Q12, Q13, Q14, Q15, Q16, Q17, Q18, Q19, Q20, Q21, Q22, Q23, Q24, Q25, Q26, Q27, Q28, Q29, Q30, Q31, Q32, Q33, Q34, Q35, Q36, Q37, Q38, Q39, Q40, Q41, Q42, Q43, Q44, Q45, Q46, Q47, Q48, Q49, Q50, Q51, Q52, Q53]), "transformType" : TransformType.ROTATION, "transformAxis" : qUnion([Q54]), "angle" : 135 * degree, "makeCopy" : false});
        }
    });
